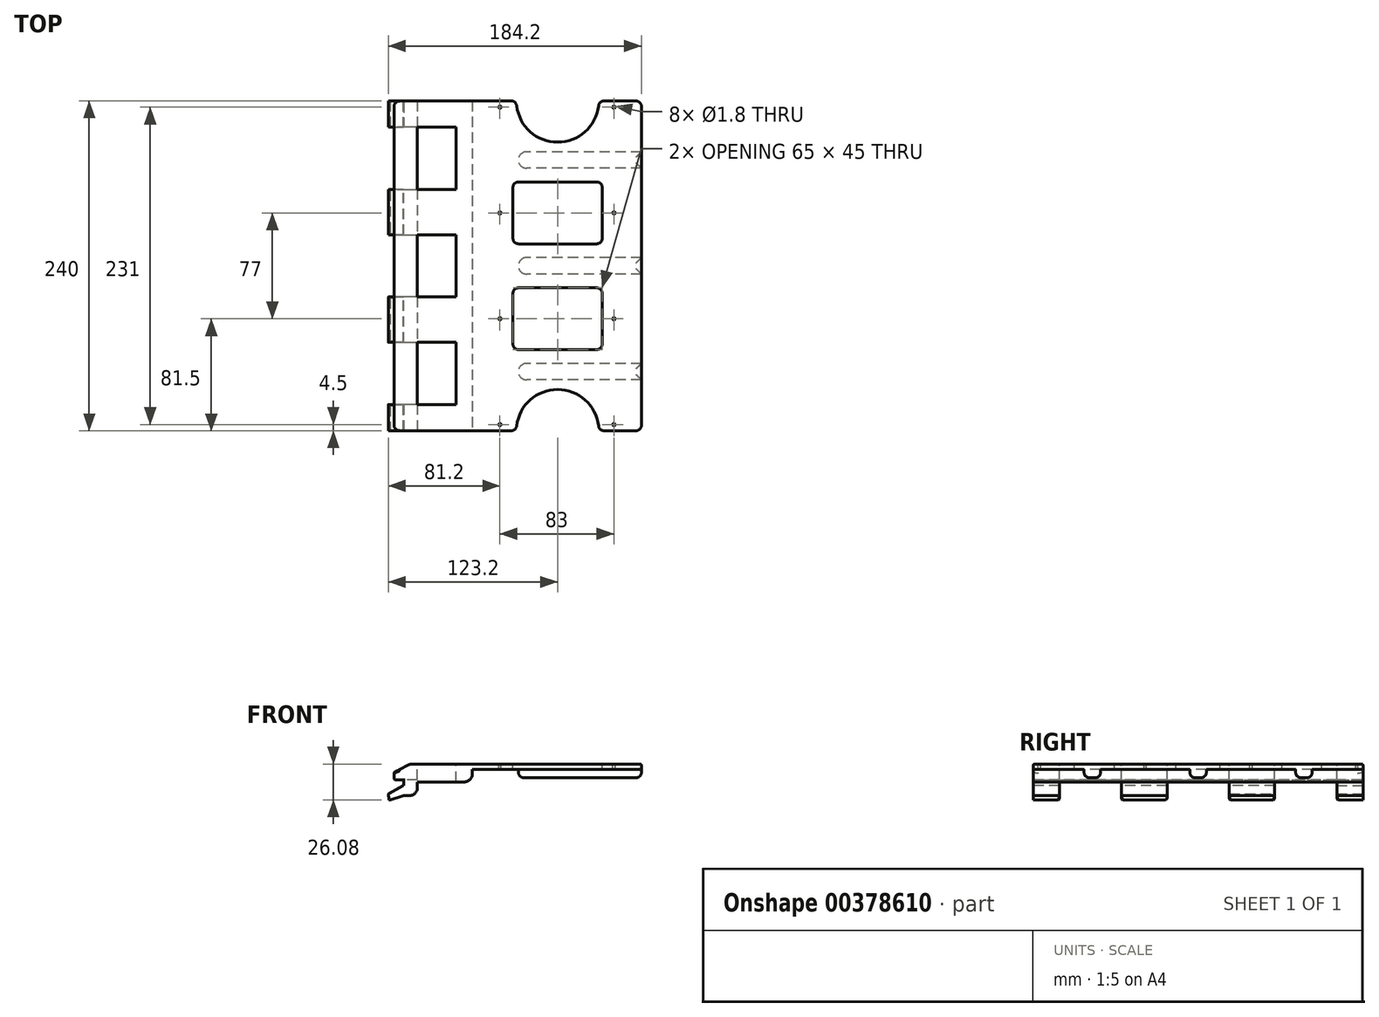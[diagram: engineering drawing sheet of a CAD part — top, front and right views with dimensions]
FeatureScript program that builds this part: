
annotation { "Feature Type Name" : "Feature", "Feature Type Description" : "" }
export const myFeature = defineFeature(function(context is Context, id is Id, definition is map)
    precondition{}
    {
        {
            var Q0;
            Q0=qCreatedBy(makeId("Top.planeOp"),FACE);
            var sketch = newSketch(context, id + "F0", { "sketchPlane" : qUnion([Q0])});
            skLineSegment(sketch, "E0", {"start": v(0, -197) * mm, "end": v(180, -197) * mm, "construction": true});
            skLineSegment(sketch, "E1", {"start": v(0, -43) * mm, "end": v(180, -43) * mm, "construction": true});
            skLineSegment(sketch, "E2", {"start": v(0, -158.5) * mm, "end": v(180, -158.5) * mm, "construction": true});
            skLineSegment(sketch, "E3", {"start": v(0, -81.5) * mm, "end": v(180, -81.5) * mm, "construction": true});
            skLineSegment(sketch, "E4", {"start": v(180, -203) * mm, "end": v(96.5, -203) * mm});
            skLineSegment(sketch, "E5", {"start": v(180, -191) * mm, "end": v(96.5, -191) * mm});
            skArc(sketch, "E6", {"start": v(96.5, -191) * mm, "mid": v(90.5, -197) * mm, "end": v(96.5, -203) * mm});
            skLineSegment(sketch, "E7", {"start": v(180, -126) * mm, "end": v(96.5, -126) * mm});
            skLineSegment(sketch, "E8", {"start": v(180, -114) * mm, "end": v(96.5, -114) * mm});
            skArc(sketch, "E9", {"start": v(96.5, -114) * mm, "mid": v(90.5, -120) * mm, "end": v(96.5, -126) * mm});
            skLineSegment(sketch, "E10", {"start": v(180, -49) * mm, "end": v(96.5, -49) * mm});
            skLineSegment(sketch, "E11", {"start": v(180, -37) * mm, "end": v(96.5, -37) * mm});
            skArc(sketch, "E12", {"start": v(96.5, -37) * mm, "mid": v(90.5, -43) * mm, "end": v(96.5, -49) * mm});
            skLineSegment(sketch, "E13", {"start": v(96.5, -240) * mm, "end": v(96.5, 0) * mm, "construction": true});
            skCircle(sketch, "E14", {"center": v(77, -158.5) * mm, "radius": 0.9 * mm});
            skCircle(sketch, "E15", {"center": v(77, -81.5) * mm, "radius": 0.9 * mm});
            skCircle(sketch, "E16", {"center": v(160, -158.5) * mm, "radius": 0.9 * mm});
            skCircle(sketch, "E17", {"center": v(160, -81.5) * mm, "radius": 0.9 * mm});
            skLineSegment(sketch, "E18.bottom", {"start": v(180, -240) * mm, "end": v(0, -240) * mm});
            skLineSegment(sketch, "E18.top", {"start": v(180, 0) * mm, "end": v(0, 0) * mm});
            skLineSegment(sketch, "E18.left", {"start": v(180, -240) * mm, "end": v(180, 0) * mm});
            skLineSegment(sketch, "E18.right", {"start": v(0, -240) * mm, "end": v(0, 0) * mm});
            skLineSegment(sketch, "E19", {"start": v(5, 0) * mm, "end": v(5, -240) * mm});
            skLineSegment(sketch, "E20", {"start": v(0, -120) * mm, "end": v(180, -120) * mm, "construction": true});
            skLineSegment(sketch, "E21", {"start": v(17, 0) * mm, "end": v(17, -240) * mm});
            skLineSegment(sketch, "E22", {"start": v(57, 0) * mm, "end": v(57, -240) * mm});
            skLineSegment(sketch, "E23", {"start": v(0, -97.4) * mm, "end": v(45, -97.4) * mm});
            skLineSegment(sketch, "E24", {"start": v(45, -97.4) * mm, "end": v(45, -142.6) * mm});
            skLineSegment(sketch, "E25", {"start": v(45, -142.6) * mm, "end": v(0, -142.6) * mm});
            skLineSegment(sketch, "E26", {"start": v(0, -175.7) * mm, "end": v(45, -175.7) * mm});
            skLineSegment(sketch, "E27", {"start": v(45, -175.7) * mm, "end": v(45, -220.9) * mm});
            skLineSegment(sketch, "E28", {"start": v(45, -220.9) * mm, "end": v(0, -220.9) * mm});
            skLineSegment(sketch, "E29", {"start": v(0, -64.3) * mm, "end": v(45, -64.3) * mm});
            skLineSegment(sketch, "E30", {"start": v(45, -64.3) * mm, "end": v(45, -19.1) * mm});
            skLineSegment(sketch, "E31", {"start": v(45, -19.1) * mm, "end": v(0, -19.1) * mm});
            skLineSegment(sketch, "E32", {"start": v(0, -235.5) * mm, "end": v(180, -235.5) * mm, "construction": true});
            skLineSegment(sketch, "E33", {"start": v(0, -4.5) * mm, "end": v(180, -4.5) * mm, "construction": true});
            skCircle(sketch, "E34", {"center": v(77, -235.5) * mm, "radius": 0.9 * mm});
            skCircle(sketch, "E35", {"center": v(77, -4.5) * mm, "radius": 0.9 * mm});
            skCircle(sketch, "E36", {"center": v(160, -4.5) * mm, "radius": 0.9 * mm});
            skCircle(sketch, "E37", {"center": v(160, -235.5) * mm, "radius": 0.9 * mm});
            skLineSegment(sketch, "E38.bottom", {"start": v(151.5, -104) * mm, "end": v(86.5, -104) * mm});
            skLineSegment(sketch, "E38.top", {"start": v(151.5, -59) * mm, "end": v(86.5, -59) * mm});
            skLineSegment(sketch, "E38.left", {"start": v(151.5, -104) * mm, "end": v(151.5, -59) * mm});
            skLineSegment(sketch, "E38.right", {"start": v(86.5, -104) * mm, "end": v(86.5, -59) * mm});
            skPoint(sketch, "E38.middle", {"position": v(119, -81.5) * mm});
            skLineSegment(sketch, "E39.bottom", {"start": v(151.5, -181) * mm, "end": v(86.5, -181) * mm});
            skLineSegment(sketch, "E39.top", {"start": v(151.5, -136) * mm, "end": v(86.5, -136) * mm});
            skLineSegment(sketch, "E39.left", {"start": v(151.5, -181) * mm, "end": v(151.5, -136) * mm});
            skLineSegment(sketch, "E39.right", {"start": v(86.5, -181) * mm, "end": v(86.5, -136) * mm});
            skPoint(sketch, "E39.middle", {"position": v(119, -158.5) * mm});
            skCircle(sketch, "E40", {"center": v(119, 0) * mm, "radius": 30 * mm});
            skCircle(sketch, "E41", {"center": v(119, -240) * mm, "radius": 30 * mm});
            skPoint(sketch, "E41.centerSnap0", {"position": v(119, -181) * mm});
            skSolve(sketch);
        }
        {
            var Q0;
            {var subQ7=sQuery(id+"F0.wireOp",EDGE,"E4");Q0=makeQuery(id+"F0.imprint","IMPRINT",FACE,{"disambiguationData":[TD([[makeQuery(id+"F0.imprint","IMPRINT",EDGE,{"derivedFrom":subQ7}),1.0]])]});}
            var Q1;
            {var subQ0=sQuery(id+"F0.wireOp",EDGE,"E4");Q1=makeQuery(id+"F0.imprint","IMPRINT",FACE,{"disambiguationData":[TD([[makeQuery(id+"F0.imprint","IMPRINT",EDGE,{"derivedFrom":subQ0}),-1.0]])]});}
            var Q2;
            {var subQ0=sQuery(id+"F0.wireOp",EDGE,"E7");Q2=makeQuery(id+"F0.imprint","IMPRINT",FACE,{"disambiguationData":[TD([[makeQuery(id+"F0.imprint","IMPRINT",EDGE,{"derivedFrom":subQ0}),-1.0]])]});}
            var Q3;
            {var subQ0=sQuery(id+"F0.wireOp",EDGE,"E10");Q3=makeQuery(id+"F0.imprint","IMPRINT",FACE,{"disambiguationData":[TD([[makeQuery(id+"F0.imprint","IMPRINT",EDGE,{"derivedFrom":subQ0}),-1.0]])]});}
            extrude(context, id + "F1", {"entities" : qUnion([Q0, Q1, Q2, Q3]), "oppositeDirection" : true, "depth" : 4 * mm});
        }
        {
            var Q0;
            {var subQ0=sQuery(id+"F0.wireOp",EDGE,"E21");Q0=makeQuery(id+"F0.imprint","IMPRINT",FACE,{"disambiguationData":[TD([[makeQuery(id+"F0.imprint","IMPRINT",EDGE,{"derivedFrom":subQ0}),1.0]])]});}
            var Q1;
            {var subQ5=sQuery(id+"F0.wireOp",EDGE,"n4lQ4PQO-9XsQ-tz0W-XekK-HpTfJCge4sbG");Q1=makeQuery(id+"F0.imprint","IMPRINT",FACE,{"disambiguationData":[TD([[makeQuery(id+"F0.imprint","IMPRINT",EDGE,{"derivedFrom":subQ5}),1.0]])]});}
            var Q2;
            {var subQ5=sQuery(id+"F0.wireOp",EDGE,"NRY2d1nv-D3un-2PJu-Z2eF-jLOu5DY2E8th");Q2=makeQuery(id+"F0.imprint","IMPRINT",FACE,{"disambiguationData":[TD([[makeQuery(id+"F0.imprint","IMPRINT",EDGE,{"derivedFrom":subQ5}),1.0]])]});}
            extrude(context, id + "F2", {"entities" : qUnion([Q0, Q1, Q2]), "operationType" : NewBodyOperationType.ADD, "oppositeDirection" : true, "depth" : 13 * mm});
        }
        {
            var Q0;
            {var subQ0=sQuery(id+"F0.wireOp",EDGE,"E19");var subQ1=sQuery(id+"F0.wireOp",EDGE,"E18.bottom");var subQ2=makeQuery(id+"F0.imprint","INTERSECT",VERTEX,{"derivedFrom":[subQ1,subQ0]});Q0=makeQuery(id+"F0.imprint","IMPRINT",FACE,{"disambiguationData":[TD([[makeQuery(id+"F0.imprint","IMPRINT",EDGE,{"disambiguationData":[TD([[subQ2,1.0]])],"derivedFrom":subQ1}),-1.0]])]});}
            var Q1;
            {var subQ0=sQuery(id+"F0.wireOp",EDGE,"E19");var subQ1=sQuery(id+"F0.wireOp",EDGE,"E18.top");var subQ2=makeQuery(id+"F0.imprint","INTERSECT",VERTEX,{"derivedFrom":[subQ1,subQ0]});Q1=makeQuery(id+"F0.imprint","IMPRINT",FACE,{"disambiguationData":[TD([[makeQuery(id+"F0.imprint","IMPRINT",EDGE,{"disambiguationData":[TD([[subQ2,1.0]])],"derivedFrom":subQ1}),1.0]])]});}
            var Q2;
            {var subQ0=sQuery(id+"F0.wireOp",EDGE,"E29");var subQ1=sQuery(id+"F0.wireOp",EDGE,"E19");var subQ2=makeQuery(id+"F0.imprint","INTERSECT",VERTEX,{"derivedFrom":[subQ1,subQ0]});Q2=makeQuery(id+"F0.imprint","IMPRINT",FACE,{"disambiguationData":[TD([[makeQuery(id+"F0.imprint","IMPRINT",EDGE,{"disambiguationData":[TD([[subQ2,-1.0]])],"derivedFrom":subQ1}),1.0]])]});}
            var Q3;
            {var subQ0=sQuery(id+"F0.wireOp",EDGE,"E25");var subQ1=sQuery(id+"F0.wireOp",EDGE,"E19");var subQ2=makeQuery(id+"F0.imprint","INTERSECT",VERTEX,{"derivedFrom":[subQ1,subQ0]});Q3=makeQuery(id+"F0.imprint","IMPRINT",FACE,{"disambiguationData":[TD([[makeQuery(id+"F0.imprint","IMPRINT",EDGE,{"disambiguationData":[TD([[subQ2,-1.0]])],"derivedFrom":subQ1}),1.0]])]});}
            extrude(context, id + "F3", {"entities" : qUnion([Q0, Q1, Q2, Q3]), "operationType" : NewBodyOperationType.ADD, "oppositeDirection" : true, "depth" : 23 * mm});
        }
        {
            var Q0;
            {var subQ0=sQuery(id+"F0.wireOp",EDGE,"E18.right");var subQ1=sQuery(id+"F0.wireOp",EDGE,"E18.bottom");var subQ2=makeQuery(id+"F0.imprint","INTERSECT",VERTEX,{"derivedFrom":[subQ1,subQ0]});Q0=makeQuery(id+"F0.imprint","IMPRINT",FACE,{"disambiguationData":[TD([[makeQuery(id+"F0.imprint","IMPRINT",EDGE,{"disambiguationData":[TD([[subQ2,1.0]])],"derivedFrom":subQ1}),-1.0]])]});}
            var Q1;
            {var subQ0=sQuery(id+"F0.wireOp",EDGE,"E18.right");var subQ1=sQuery(id+"F0.wireOp",EDGE,"E18.top");var subQ2=makeQuery(id+"F0.imprint","INTERSECT",VERTEX,{"derivedFrom":[subQ1,subQ0]});Q1=makeQuery(id+"F0.imprint","IMPRINT",FACE,{"disambiguationData":[TD([[makeQuery(id+"F0.imprint","IMPRINT",EDGE,{"disambiguationData":[TD([[subQ2,1.0]])],"derivedFrom":subQ1}),1.0]])]});}
            var Q2;
            {var subQ0=sQuery(id+"F0.wireOp",EDGE,"E25");var subQ1=sQuery(id+"F0.wireOp",EDGE,"E18.right");var subQ2=makeQuery(id+"F0.imprint","INTERSECT",VERTEX,{"derivedFrom":[subQ1,subQ0]});Q2=makeQuery(id+"F0.imprint","IMPRINT",FACE,{"disambiguationData":[TD([[makeQuery(id+"F0.imprint","IMPRINT",EDGE,{"disambiguationData":[TD([[subQ2,1.0]])],"derivedFrom":subQ1}),-1.0]])]});}
            var Q3;
            {var subQ0=sQuery(id+"F0.wireOp",EDGE,"E23");var subQ1=sQuery(id+"F0.wireOp",EDGE,"E18.right");var subQ2=makeQuery(id+"F0.imprint","INTERSECT",VERTEX,{"derivedFrom":[subQ1,subQ0]});Q3=makeQuery(id+"F0.imprint","IMPRINT",FACE,{"disambiguationData":[TD([[makeQuery(id+"F0.imprint","IMPRINT",EDGE,{"disambiguationData":[TD([[subQ2,-1.0]])],"derivedFrom":subQ1}),-1.0]])]});}
            var Q4;
            {var subQ0=sQuery(id+"F0.wireOp",EDGE,"E26");var subQ1=sQuery(id+"F0.wireOp",EDGE,"E18.right");var subQ2=makeQuery(id+"F0.imprint","INTERSECT",VERTEX,{"derivedFrom":[subQ1,subQ0]});Q4=makeQuery(id+"F0.imprint","IMPRINT",FACE,{"disambiguationData":[TD([[makeQuery(id+"F0.imprint","IMPRINT",EDGE,{"disambiguationData":[TD([[subQ2,1.0]])],"derivedFrom":subQ1}),-1.0]])]});}
            var Q5;
            {var subQ0=sQuery(id+"F0.wireOp",EDGE,"E23");var subQ1=sQuery(id+"F0.wireOp",EDGE,"E18.right");var subQ2=makeQuery(id+"F0.imprint","INTERSECT",VERTEX,{"derivedFrom":[subQ1,subQ0]});Q5=makeQuery(id+"F0.imprint","IMPRINT",FACE,{"disambiguationData":[TD([[makeQuery(id+"F0.imprint","IMPRINT",EDGE,{"disambiguationData":[TD([[subQ2,1.0]])],"derivedFrom":subQ1}),-1.0]])]});}
            var Q6;
            {var subQ0=sQuery(id+"F0.wireOp",EDGE,"E29");var subQ1=sQuery(id+"F0.wireOp",EDGE,"E18.right");var subQ2=makeQuery(id+"F0.imprint","INTERSECT",VERTEX,{"derivedFrom":[subQ1,subQ0]});Q6=makeQuery(id+"F0.imprint","IMPRINT",FACE,{"disambiguationData":[TD([[makeQuery(id+"F0.imprint","IMPRINT",EDGE,{"disambiguationData":[TD([[subQ2,-1.0]])],"derivedFrom":subQ1}),-1.0]])]});}
            var Q7;
            {var subQ0=sQuery(id+"F0.wireOp",EDGE,"E26");var subQ1=sQuery(id+"F0.wireOp",EDGE,"E19");var subQ2=makeQuery(id+"F0.imprint","INTERSECT",VERTEX,{"derivedFrom":[subQ1,subQ0]});Q7=makeQuery(id+"F0.imprint","IMPRINT",FACE,{"disambiguationData":[TD([[makeQuery(id+"F0.imprint","IMPRINT",EDGE,{"disambiguationData":[TD([[subQ2,-1.0]])],"derivedFrom":subQ1}),1.0]])]});}
            var Q8;
            {var subQ0=sQuery(id+"F0.wireOp",EDGE,"E23");var subQ1=sQuery(id+"F0.wireOp",EDGE,"E19");var subQ2=makeQuery(id+"F0.imprint","INTERSECT",VERTEX,{"derivedFrom":[subQ1,subQ0]});Q8=makeQuery(id+"F0.imprint","IMPRINT",FACE,{"disambiguationData":[TD([[makeQuery(id+"F0.imprint","IMPRINT",EDGE,{"disambiguationData":[TD([[subQ2,-1.0]])],"derivedFrom":subQ1}),1.0]])]});}
            var Q9;
            {var subQ0=sQuery(id+"F0.wireOp",EDGE,"E31");var subQ1=sQuery(id+"F0.wireOp",EDGE,"E19");var subQ2=makeQuery(id+"F0.imprint","INTERSECT",VERTEX,{"derivedFrom":[subQ1,subQ0]});Q9=makeQuery(id+"F0.imprint","IMPRINT",FACE,{"disambiguationData":[TD([[makeQuery(id+"F0.imprint","IMPRINT",EDGE,{"disambiguationData":[TD([[subQ2,-1.0]])],"derivedFrom":subQ1}),1.0]])]});}
            var Q10;
            Q10=makeQuery(id+"F2.opExtrude","CAP_FACE",FACE,{"disambiguationData":[OSD([sQuery(id+"F0.wireOp",EDGE,"E14"),sQuery(id+"F0.wireOp",EDGE,"E15"),sQuery(id+"F0.wireOp",EDGE,"E18.bottom"),sQuery(id+"F0.wireOp",EDGE,"E18.top"),sQuery(id+"F0.wireOp",EDGE,"E21"),sQuery(id+"F0.wireOp",EDGE,"E22")])],"isStart":false});
            extrude(context, id + "F4", {"entities" : qUnion([Q0, Q1, Q2, Q3, Q4, Q5, Q6, Q7, Q8, Q9]), "operationType" : NewBodyOperationType.ADD, "oppositeDirection" : true, "endBoundEntityFace" : qUnion([Q10]), "depth" : 11.5 * mm});
        }
        {
            var Q0;
            {var subQ0=sQuery(id+"F0.wireOp",EDGE,"E18.bottom");Q0=makeQuery(id+"F4.boolean.opBoolean","MERGE",FACE,{"derivedFrom":[makeQuery(id+"F3.boolean.opBoolean","MERGE",FACE,{"derivedFrom":[makeQuery(id+"F2.boolean.opBoolean","MERGE",FACE,{"derivedFrom":[makeQuery(id+"F1.opExtrude","SWEPT_FACE",FACE,{"disambiguationData":[OSD([subQ0])]}),makeQuery(id+"F2.opExtrude","SWEPT_FACE",FACE,{"disambiguationData":[OSD([subQ0])]})]}),makeQuery(id+"F3.opExtrude","SWEPT_FACE",FACE,{"disambiguationData":[OSD([subQ0])]})]}),makeQuery(id+"F4.opExtrude","SWEPT_FACE",FACE,{"disambiguationData":[OSD([subQ0])]})]});}
            var sketch = newSketch(context, id + "F5", { "sketchPlane" : qUnion([Q0])});
            skLineSegment(sketch, "E42.bottom", {"start": v(5, -11.5) * mm, "end": v(7, -11.5) * mm});
            skLineSegment(sketch, "E42.top", {"start": v(5, -15.5) * mm, "end": v(7, -15.5) * mm});
            skLineSegment(sketch, "E42.left", {"start": v(5, -11.5) * mm, "end": v(5, -15.5) * mm});
            skLineSegment(sketch, "E42.right", {"start": v(7, -11.5) * mm, "end": v(7, -15.5) * mm});
            skSolve(sketch);
        }
        {
            var Q0;
            Q0=makeQuery(id+"F5.imprint","IMPRINT",FACE,{"disambiguationData":[TD([[makeQuery(id+"F5.imprint","IMPRINT",EDGE,{"derivedFrom":sQuery(id+"F5.wireOp",EDGE,"E42.bottom")}),-1.0]])]});
            var Q1;
            {var subQ0=sQuery(id+"F0.wireOp",EDGE,"E18.top");Q1=makeQuery(id+"F4.boolean.opBoolean","MERGE",FACE,{"derivedFrom":[makeQuery(id+"F3.boolean.opBoolean","MERGE",FACE,{"derivedFrom":[makeQuery(id+"F2.boolean.opBoolean","MERGE",FACE,{"derivedFrom":[makeQuery(id+"F1.opExtrude","SWEPT_FACE",FACE,{"disambiguationData":[OSD([subQ0])]}),makeQuery(id+"F2.opExtrude","SWEPT_FACE",FACE,{"disambiguationData":[OSD([subQ0])]})]}),makeQuery(id+"F3.opExtrude","SWEPT_FACE",FACE,{"disambiguationData":[OSD([subQ0])]})]}),makeQuery(id+"F4.opExtrude","SWEPT_FACE",FACE,{"disambiguationData":[OSD([subQ0])]})]});}
            extrude(context, id + "F6", {"entities" : qUnion([Q0]), "operationType" : NewBodyOperationType.REMOVE, "oppositeDirection" : true, "endBoundEntityFace" : qUnion([Q1]), "depth" : 300 * mm});
        }
        {
            var Q0;
            {var subQ0=sQuery(id+"F0.wireOp",EDGE,"E4");Q0=makeQuery(id+"F0.imprint","IMPRINT",FACE,{"disambiguationData":[TD([[makeQuery(id+"F0.imprint","IMPRINT",EDGE,{"derivedFrom":subQ0}),-1.0]])]});}
            var Q1;
            {var subQ0=sQuery(id+"F0.wireOp",EDGE,"E7");Q1=makeQuery(id+"F0.imprint","IMPRINT",FACE,{"disambiguationData":[TD([[makeQuery(id+"F0.imprint","IMPRINT",EDGE,{"derivedFrom":subQ0}),-1.0]])]});}
            var Q2;
            {var subQ0=sQuery(id+"F0.wireOp",EDGE,"E10");Q2=makeQuery(id+"F0.imprint","IMPRINT",FACE,{"disambiguationData":[TD([[makeQuery(id+"F0.imprint","IMPRINT",EDGE,{"derivedFrom":subQ0}),-1.0]])]});}
            extrude(context, id + "F7", {"entities" : qUnion([Q0, Q1, Q2]), "operationType" : NewBodyOperationType.ADD, "oppositeDirection" : true, "depth" : 10 * mm});
        }
        {
            var Q0;
            Q0=makeQuery(id+"F7.opExtrude","CAP_FACE",FACE,{"disambiguationData":[OSD([sQuery(id+"F0.wireOp",EDGE,"E10"),sQuery(id+"F0.wireOp",EDGE,"E11"),sQuery(id+"F0.wireOp",EDGE,"E12"),sQuery(id+"F0.wireOp",EDGE,"E18.left")])],"isStart":false});
            var Q1;
            Q1=makeQuery(id+"F7.opExtrude","CAP_FACE",FACE,{"disambiguationData":[OSD([sQuery(id+"F0.wireOp",EDGE,"E7"),sQuery(id+"F0.wireOp",EDGE,"E8"),sQuery(id+"F0.wireOp",EDGE,"E9"),sQuery(id+"F0.wireOp",EDGE,"E18.left")])],"isStart":false});
            var Q2;
            Q2=makeQuery(id+"F7.opExtrude","CAP_FACE",FACE,{"disambiguationData":[OSD([sQuery(id+"F0.wireOp",EDGE,"E4"),sQuery(id+"F0.wireOp",EDGE,"E5"),sQuery(id+"F0.wireOp",EDGE,"E6"),sQuery(id+"F0.wireOp",EDGE,"E18.left")])],"isStart":false});
            var Q3;
            Q3=makeQuery(id+"F1.opExtrude","SWEPT_EDGE",EDGE,{"disambiguationData":[OSD([sQuery(id+"F0.wireOp",EDGE,"E38.top"),sQuery(id+"F0.wireOp",EDGE,"E38.right")])]});
            var Q4;
            Q4=makeQuery(id+"F1.opExtrude","SWEPT_EDGE",EDGE,{"disambiguationData":[OSD([sQuery(id+"F0.wireOp",EDGE,"E38.bottom"),sQuery(id+"F0.wireOp",EDGE,"E38.right")])]});
            var Q5;
            Q5=makeQuery(id+"F1.opExtrude","SWEPT_EDGE",EDGE,{"disambiguationData":[OSD([sQuery(id+"F0.wireOp",EDGE,"E38.top"),sQuery(id+"F0.wireOp",EDGE,"E38.left")])]});
            var Q6;
            Q6=makeQuery(id+"F1.opExtrude","SWEPT_EDGE",EDGE,{"disambiguationData":[OSD([sQuery(id+"F0.wireOp",EDGE,"E38.bottom"),sQuery(id+"F0.wireOp",EDGE,"E38.left")])]});
            var Q7;
            Q7=makeQuery(id+"F1.opExtrude","SWEPT_EDGE",EDGE,{"disambiguationData":[OSD([sQuery(id+"F0.wireOp",EDGE,"E39.top"),sQuery(id+"F0.wireOp",EDGE,"E39.left")])]});
            var Q8;
            {var subQ0=sQuery(id+"F0.wireOp",EDGE,"E41");var subQ1=sQuery(id+"F0.wireOp",EDGE,"E18.bottom");Q8=makeQuery(id+"F1.opExtrude","SWEPT_EDGE",EDGE,{"disambiguationData":[OSD([subQ1,subQ0]),TDD([makeQuery(id+"F0.imprint","INTERSECT",VERTEX,{"disambiguationData":[OD(1.0)],"derivedFrom":[subQ1,subQ0]})])]});}
            var Q9;
            Q9=makeQuery(id+"F1.opExtrude","SWEPT_EDGE",EDGE,{"disambiguationData":[OSD([sQuery(id+"F0.wireOp",EDGE,"E39.bottom"),sQuery(id+"F0.wireOp",EDGE,"E39.right")])]});
            var Q10;
            Q10=makeQuery(id+"F1.opExtrude","SWEPT_EDGE",EDGE,{"disambiguationData":[OSD([sQuery(id+"F0.wireOp",EDGE,"E39.top"),sQuery(id+"F0.wireOp",EDGE,"E39.right")])]});
            var Q11;
            {var subQ0=sQuery(id+"F0.wireOp",EDGE,"E40");var subQ1=sQuery(id+"F0.wireOp",EDGE,"E18.top");Q11=makeQuery(id+"F1.opExtrude","SWEPT_EDGE",EDGE,{"disambiguationData":[OSD([subQ1,subQ0]),TDD([makeQuery(id+"F0.imprint","INTERSECT",VERTEX,{"disambiguationData":[OD(1.0)],"derivedFrom":[subQ1,subQ0]})])]});}
            var Q12;
            {var subQ0=sQuery(id+"F0.wireOp",EDGE,"E40");var subQ1=sQuery(id+"F0.wireOp",EDGE,"E18.top");Q12=makeQuery(id+"F1.opExtrude","SWEPT_EDGE",EDGE,{"disambiguationData":[OSD([subQ1,subQ0]),TDD([makeQuery(id+"F0.imprint","INTERSECT",VERTEX,{"disambiguationData":[OD(0.0)],"derivedFrom":[subQ1,subQ0]})])]});}
            var Q13;
            Q13=makeQuery(id+"F1.opExtrude","SWEPT_EDGE",EDGE,{"disambiguationData":[OSD([sQuery(id+"F0.wireOp",EDGE,"E39.bottom"),sQuery(id+"F0.wireOp",EDGE,"E39.left")])]});
            var Q14;
            {var subQ0=sQuery(id+"F0.wireOp",EDGE,"E41");var subQ1=sQuery(id+"F0.wireOp",EDGE,"E18.bottom");Q14=makeQuery(id+"F1.opExtrude","SWEPT_EDGE",EDGE,{"disambiguationData":[OSD([subQ1,subQ0]),TDD([makeQuery(id+"F0.imprint","INTERSECT",VERTEX,{"disambiguationData":[OD(0.0)],"derivedFrom":[subQ1,subQ0]})])]});}
            var Q15;
            Q15=makeQuery(id+"F1.opExtrude","SWEPT_EDGE",EDGE,{"disambiguationData":[OSD([sQuery(id+"F0.wireOp",EDGE,"E18.bottom"),sQuery(id+"F0.wireOp",EDGE,"E18.left")])]});
            var Q16;
            Q16=makeQuery(id+"F1.opExtrude","SWEPT_EDGE",EDGE,{"disambiguationData":[OSD([sQuery(id+"F0.wireOp",EDGE,"E18.top"),sQuery(id+"F0.wireOp",EDGE,"E18.left")])]});
            var Q17;
            Q17=makeQuery(id+"F4.opExtrude","SWEPT_EDGE",EDGE,{"disambiguationData":[OSD([sQuery(id+"F0.wireOp",EDGE,"E18.top"),sQuery(id+"F0.wireOp",EDGE,"E18.right")])]});
            var Q18;
            Q18=makeQuery(id+"F4.opExtrude","SWEPT_EDGE",EDGE,{"disambiguationData":[OSD([sQuery(id+"F0.wireOp",EDGE,"E18.bottom"),sQuery(id+"F0.wireOp",EDGE,"E18.right")])]});
            fillet(context, id + "F8", {"entities" : qUnion([Q0, Q1, Q2, Q3, Q4, Q5, Q6, Q7, Q8, Q9, Q10, Q11, Q12, Q13, Q14, Q15, Q16, Q17, Q18]), "radius" : 4 * mm, "tangentPropagation" : true, "allowEdgeOverflow" : false});
        }
        {
            var Q0;
            Q0=makeQuery(id+"F4.opExtrude","CAP_EDGE",EDGE,{"disambiguationData":[OSD([sQuery(id+"F0.wireOp",EDGE,"E18.right")])],"isStart":true});
            chamfer(context, id + "F9", {"entities" : qUnion([Q0]), "chamferType" : ChamferType.TWO_OFFSETS, "width1" : 6 * mm, "oppositeDirection" : false, "width2" : 12 * mm});
        }
        {
            var Q0;
            {var subQ0=sQuery(id+"F0.wireOp",EDGE,"E19");Q0=makeQuery(id+"F3.opExtrude","CAP_EDGE",EDGE,{"disambiguationData":[OSD([subQ0]),TDD([makeQuery(id+"F0.imprint","IMPRINT",EDGE,{"disambiguationData":[TD([[makeQuery(id+"F0.imprint","INTERSECT",VERTEX,{"derivedFrom":[sQuery(id+"F0.wireOp",EDGE,"E18.bottom"),subQ0]}),1.0]])],"derivedFrom":subQ0})])],"isStart":false});}
            var Q1;
            {var subQ0=sQuery(id+"F0.wireOp",EDGE,"E19");Q1=makeQuery(id+"F3.opExtrude","CAP_EDGE",EDGE,{"disambiguationData":[OSD([subQ0]),TDD([makeQuery(id+"F0.imprint","IMPRINT",EDGE,{"disambiguationData":[TD([[makeQuery(id+"F0.imprint","INTERSECT",VERTEX,{"derivedFrom":[subQ0,sQuery(id+"F0.wireOp",EDGE,"E25")]}),-1.0]])],"derivedFrom":subQ0})])],"isStart":false});}
            var Q2;
            {var subQ0=sQuery(id+"F0.wireOp",EDGE,"E19");Q2=makeQuery(id+"F3.opExtrude","CAP_EDGE",EDGE,{"disambiguationData":[OSD([subQ0]),TDD([makeQuery(id+"F0.imprint","IMPRINT",EDGE,{"disambiguationData":[TD([[makeQuery(id+"F0.imprint","INTERSECT",VERTEX,{"derivedFrom":[subQ0,sQuery(id+"F0.wireOp",EDGE,"E29")]}),-1.0]])],"derivedFrom":subQ0})])],"isStart":false});}
            var Q3;
            {var subQ0=sQuery(id+"F0.wireOp",EDGE,"E19");Q3=makeQuery(id+"F3.opExtrude","CAP_EDGE",EDGE,{"disambiguationData":[OSD([subQ0]),TDD([makeQuery(id+"F0.imprint","IMPRINT",EDGE,{"disambiguationData":[TD([[makeQuery(id+"F0.imprint","INTERSECT",VERTEX,{"derivedFrom":[sQuery(id+"F0.wireOp",EDGE,"E18.top"),subQ0]}),-1.0]])],"derivedFrom":subQ0})])],"isStart":false});}
            chamfer(context, id + "F10", {"entities" : qUnion([Q0, Q1, Q2, Q3]), "chamferType" : ChamferType.TWO_OFFSETS, "width1" : 20 * mm, "oppositeDirection" : false, "width2" : 2 * mm});
        }
        {
            var Q0;
            {var subQ0=sQuery(id+"F0.wireOp",EDGE,"E19");Q0=makeQuery(id+"F10.opChamfer","BLEND_FACE",FACE,{"disambiguationData":[OSD([subQ0]),TDD([makeQuery(id+"F3.opExtrude","CAP_EDGE",EDGE,{"disambiguationData":[OSD([subQ0]),TDD([makeQuery(id+"F0.imprint","IMPRINT",EDGE,{"disambiguationData":[TD([[makeQuery(id+"F0.imprint","INTERSECT",VERTEX,{"derivedFrom":[sQuery(id+"F0.wireOp",EDGE,"E18.bottom"),subQ0]}),1.0]])],"derivedFrom":subQ0})])],"isStart":false})])]});}
            var Q1;
            {var subQ0=sQuery(id+"F0.wireOp",EDGE,"E19");Q1=makeQuery(id+"F10.opChamfer","BLEND_FACE",FACE,{"disambiguationData":[OSD([subQ0]),TDD([makeQuery(id+"F3.opExtrude","CAP_EDGE",EDGE,{"disambiguationData":[OSD([subQ0]),TDD([makeQuery(id+"F0.imprint","IMPRINT",EDGE,{"disambiguationData":[TD([[makeQuery(id+"F0.imprint","INTERSECT",VERTEX,{"derivedFrom":[subQ0,sQuery(id+"F0.wireOp",EDGE,"E25")]}),-1.0]])],"derivedFrom":subQ0})])],"isStart":false})])]});}
            var Q2;
            {var subQ0=sQuery(id+"F0.wireOp",EDGE,"E19");Q2=makeQuery(id+"F10.opChamfer","BLEND_FACE",FACE,{"disambiguationData":[OSD([subQ0]),TDD([makeQuery(id+"F3.opExtrude","CAP_EDGE",EDGE,{"disambiguationData":[OSD([subQ0]),TDD([makeQuery(id+"F0.imprint","IMPRINT",EDGE,{"disambiguationData":[TD([[makeQuery(id+"F0.imprint","INTERSECT",VERTEX,{"derivedFrom":[subQ0,sQuery(id+"F0.wireOp",EDGE,"E29")]}),-1.0]])],"derivedFrom":subQ0})])],"isStart":false})])]});}
            var Q3;
            {var subQ0=sQuery(id+"F0.wireOp",EDGE,"E19");Q3=makeQuery(id+"F10.opChamfer","BLEND_FACE",FACE,{"disambiguationData":[OSD([subQ0]),TDD([makeQuery(id+"F3.opExtrude","CAP_EDGE",EDGE,{"disambiguationData":[OSD([subQ0]),TDD([makeQuery(id+"F0.imprint","IMPRINT",EDGE,{"disambiguationData":[TD([[makeQuery(id+"F0.imprint","INTERSECT",VERTEX,{"derivedFrom":[sQuery(id+"F0.wireOp",EDGE,"E18.top"),subQ0]}),-1.0]])],"derivedFrom":subQ0})])],"isStart":false})])]});}
            extrude(context, id + "F11", {"entities" : qUnion([Q0, Q1, Q2, Q3]), "operationType" : NewBodyOperationType.ADD, "depth" : 7 * mm});
        }
        {
            var Q0;
            {var subQ0=sQuery(id+"F0.wireOp",EDGE,"E19");Q0=makeQuery(id+"F11.opExtrude","CAP_FACE",FACE,{"disambiguationData":[OSD([subQ0]),TDD([makeQuery(id+"F10.opChamfer","BLEND_FACE",FACE,{"disambiguationData":[OSD([subQ0]),TDD([makeQuery(id+"F3.opExtrude","CAP_EDGE",EDGE,{"disambiguationData":[OSD([subQ0]),TDD([makeQuery(id+"F0.imprint","IMPRINT",EDGE,{"disambiguationData":[TD([[makeQuery(id+"F0.imprint","INTERSECT",VERTEX,{"derivedFrom":[sQuery(id+"F0.wireOp",EDGE,"E18.bottom"),subQ0]}),1.0]])],"derivedFrom":subQ0})])],"isStart":false})])]})])],"isStart":false});}
            var Q1;
            {var subQ0=sQuery(id+"F0.wireOp",EDGE,"E19");Q1=makeQuery(id+"F11.opExtrude","CAP_FACE",FACE,{"disambiguationData":[OSD([subQ0]),TDD([makeQuery(id+"F10.opChamfer","BLEND_FACE",FACE,{"disambiguationData":[OSD([subQ0]),TDD([makeQuery(id+"F3.opExtrude","CAP_EDGE",EDGE,{"disambiguationData":[OSD([subQ0]),TDD([makeQuery(id+"F0.imprint","IMPRINT",EDGE,{"disambiguationData":[TD([[makeQuery(id+"F0.imprint","INTERSECT",VERTEX,{"derivedFrom":[subQ0,sQuery(id+"F0.wireOp",EDGE,"E25")]}),-1.0]])],"derivedFrom":subQ0})])],"isStart":false})])]})])],"isStart":false});}
            var Q2;
            {var subQ0=sQuery(id+"F0.wireOp",EDGE,"E19");Q2=makeQuery(id+"F11.opExtrude","CAP_FACE",FACE,{"disambiguationData":[OSD([subQ0]),TDD([makeQuery(id+"F10.opChamfer","BLEND_FACE",FACE,{"disambiguationData":[OSD([subQ0]),TDD([makeQuery(id+"F3.opExtrude","CAP_EDGE",EDGE,{"disambiguationData":[OSD([subQ0]),TDD([makeQuery(id+"F0.imprint","IMPRINT",EDGE,{"disambiguationData":[TD([[makeQuery(id+"F0.imprint","INTERSECT",VERTEX,{"derivedFrom":[subQ0,sQuery(id+"F0.wireOp",EDGE,"E29")]}),-1.0]])],"derivedFrom":subQ0})])],"isStart":false})])]})])],"isStart":false});}
            var Q3;
            {var subQ0=sQuery(id+"F0.wireOp",EDGE,"E19");Q3=makeQuery(id+"F11.opExtrude","CAP_FACE",FACE,{"disambiguationData":[OSD([subQ0]),TDD([makeQuery(id+"F10.opChamfer","BLEND_FACE",FACE,{"disambiguationData":[OSD([subQ0]),TDD([makeQuery(id+"F3.opExtrude","CAP_EDGE",EDGE,{"disambiguationData":[OSD([subQ0]),TDD([makeQuery(id+"F0.imprint","IMPRINT",EDGE,{"disambiguationData":[TD([[makeQuery(id+"F0.imprint","INTERSECT",VERTEX,{"derivedFrom":[sQuery(id+"F0.wireOp",EDGE,"E18.top"),subQ0]}),-1.0]])],"derivedFrom":subQ0})])],"isStart":false})])]})])],"isStart":false});}
            extrude(context, id + "F12", {"entities" : qUnion([Q0, Q1, Q2, Q3]), "operationType" : NewBodyOperationType.ADD, "depth" : 4 * mm});
        }
        {
            var Q0;
            Q0=makeQuery(id+"F12.opExtrude","CAP_EDGE",EDGE,{"disambiguationData":[OSD([sQuery(id+"F0.wireOp",EDGE,"E19"),sQuery(id+"F5.wireOp",EDGE,"E42.top")])],"isStart":false});
            chamfer(context, id + "F13", {"entities" : qUnion([Q0]), "chamferType" : ChamferType.TWO_OFFSETS, "width1" : 11.5 * mm, "oppositeDirection" : false, "width2" : 5 * mm, "tangentPropagation" : true});
        }
        {
            var Q0;
            {var subQ0=sQuery(id+"F0.wireOp",EDGE,"E21");Q0=makeQuery(id+"F3.opExtrude","CAP_EDGE",EDGE,{"disambiguationData":[OSD([subQ0]),TDD([makeQuery(id+"F0.imprint","IMPRINT",EDGE,{"disambiguationData":[TD([[makeQuery(id+"F0.imprint","INTERSECT",VERTEX,{"derivedFrom":[subQ0,sQuery(id+"F0.wireOp",EDGE,"E25")]}),-1.0]])],"derivedFrom":subQ0})])],"isStart":false});}
            var Q1;
            Q1=makeQuery(id+"F2.opExtrude","CAP_EDGE",EDGE,{"disambiguationData":[OSD([sQuery(id+"F0.wireOp",EDGE,"E22")])],"isStart":false});
            var Q2;
            {var subQ0=sQuery(id+"F0.wireOp",EDGE,"E21");Q2=makeQuery(id+"F3.opExtrude","CAP_EDGE",EDGE,{"disambiguationData":[OSD([subQ0]),TDD([makeQuery(id+"F0.imprint","IMPRINT",EDGE,{"disambiguationData":[TD([[makeQuery(id+"F0.imprint","INTERSECT",VERTEX,{"derivedFrom":[subQ0,sQuery(id+"F0.wireOp",EDGE,"E29")]}),-1.0]])],"derivedFrom":subQ0})])],"isStart":false});}
            var Q3;
            {var subQ0=sQuery(id+"F0.wireOp",EDGE,"E21");Q3=makeQuery(id+"F3.opExtrude","CAP_EDGE",EDGE,{"disambiguationData":[OSD([subQ0]),TDD([makeQuery(id+"F0.imprint","IMPRINT",EDGE,{"disambiguationData":[TD([[makeQuery(id+"F0.imprint","INTERSECT",VERTEX,{"derivedFrom":[sQuery(id+"F0.wireOp",EDGE,"E18.top"),subQ0]}),-1.0]])],"derivedFrom":subQ0})])],"isStart":false});}
            var Q4;
            {var subQ0=sQuery(id+"F0.wireOp",EDGE,"E21");Q4=makeQuery(id+"F3.opExtrude","CAP_EDGE",EDGE,{"disambiguationData":[OSD([subQ0]),TDD([makeQuery(id+"F0.imprint","IMPRINT",EDGE,{"disambiguationData":[TD([[makeQuery(id+"F0.imprint","INTERSECT",VERTEX,{"derivedFrom":[sQuery(id+"F0.wireOp",EDGE,"E18.bottom"),subQ0]}),1.0]])],"derivedFrom":subQ0})])],"isStart":false});}
            fillet(context, id + "F14", {"entities" : qUnion([Q0, Q1, Q2, Q3, Q4]), "radius" : 6 * mm, "allowEdgeOverflow" : false});
        }
        {
            var Q0;
            {var subQ0=sQuery(id+"F0.wireOp",EDGE,"E28");var subQ1=sQuery(id+"F0.wireOp",EDGE,"E21");var subQ2=sQuery(id+"F0.wireOp",EDGE,"E19");var subQ3=sQuery(id+"F0.wireOp",EDGE,"E18.bottom");Q0=makeQuery(id+"F12.boolean.opBoolean","MERGE",FACE,{"derivedFrom":[makeQuery(id+"F11.opExtrude","SWEPT_FACE",FACE,{"disambiguationData":[OSD([subQ3,subQ2,subQ1,subQ0])]}),makeQuery(id+"F12.opExtrude","SWEPT_FACE",FACE,{"disambiguationData":[OSD([subQ3,subQ2,subQ1,subQ0])]})]});}
            var Q1;
            {var subQ0=sQuery(id+"F0.wireOp",EDGE,"E26");var subQ1=sQuery(id+"F0.wireOp",EDGE,"E25");var subQ2=sQuery(id+"F0.wireOp",EDGE,"E21");var subQ3=sQuery(id+"F0.wireOp",EDGE,"E19");Q1=makeQuery(id+"F12.boolean.opBoolean","MERGE",FACE,{"derivedFrom":[makeQuery(id+"F11.opExtrude","SWEPT_FACE",FACE,{"disambiguationData":[OSD([subQ3,subQ2,subQ1,subQ0])]}),makeQuery(id+"F12.opExtrude","SWEPT_FACE",FACE,{"disambiguationData":[OSD([subQ3,subQ2,subQ1,subQ0])]})]});}
            var Q2;
            {var subQ0=sQuery(id+"F0.wireOp",EDGE,"E29");var subQ1=sQuery(id+"F0.wireOp",EDGE,"E23");var subQ2=sQuery(id+"F0.wireOp",EDGE,"E21");var subQ3=sQuery(id+"F0.wireOp",EDGE,"E19");Q2=makeQuery(id+"F12.boolean.opBoolean","MERGE",FACE,{"derivedFrom":[makeQuery(id+"F11.opExtrude","SWEPT_FACE",FACE,{"disambiguationData":[OSD([subQ3,subQ2,subQ1,subQ0])]}),makeQuery(id+"F12.opExtrude","SWEPT_FACE",FACE,{"disambiguationData":[OSD([subQ3,subQ2,subQ1,subQ0])]})]});}
            var Q3;
            {var subQ0=sQuery(id+"F0.wireOp",EDGE,"E31");var subQ1=sQuery(id+"F0.wireOp",EDGE,"E21");var subQ2=sQuery(id+"F0.wireOp",EDGE,"E19");var subQ3=sQuery(id+"F0.wireOp",EDGE,"E18.top");Q3=makeQuery(id+"F12.boolean.opBoolean","MERGE",FACE,{"derivedFrom":[makeQuery(id+"F11.opExtrude","SWEPT_FACE",FACE,{"disambiguationData":[OSD([subQ3,subQ2,subQ1,subQ0])]}),makeQuery(id+"F12.opExtrude","SWEPT_FACE",FACE,{"disambiguationData":[OSD([subQ3,subQ2,subQ1,subQ0])]})]});}
            extrude(context, id + "F15", {"entities" : qUnion([Q0, Q1, Q2, Q3]), "operationType" : NewBodyOperationType.ADD, "depth" : 2 * mm});
        }
        {
            var Q0;
            {var subQ0=sQuery(id+"F0.wireOp",EDGE,"E19");var subQ1=sQuery(id+"F0.wireOp",EDGE,"E18.right");var subQ2=sQuery(id+"F0.wireOp",EDGE,"E18.top");var subQ3=sQuery(id+"F0.wireOp",EDGE,"E18.bottom");var subQ4=sQuery(id+"F0.wireOp",EDGE,"E26");var subQ5=sQuery(id+"F0.wireOp",EDGE,"E25");var subQ6=sQuery(id+"F0.wireOp",EDGE,"E21");var subQ7=sQuery(id+"F0.wireOp",EDGE,"E29");var subQ8=sQuery(id+"F0.wireOp",EDGE,"E23");var subQ9=sQuery(id+"F0.wireOp",EDGE,"E31");var subQ10=sQuery(id+"F0.wireOp",EDGE,"E28");var subQ11=sQuery(id+"F0.wireOp",EDGE,"E22");Q0=makeQuery(id+"F9.opChamfer","BLEND_EDGE",EDGE,{"disambiguationData":[OD(2.0)],"blendedFrom":[makeQuery(id+"F4.opExtrude","CAP_EDGE",EDGE,{"disambiguationData":[OSD([subQ1])],"isStart":true}),makeQuery(id+"F4.boolean.opBoolean","MERGE",FACE,{"derivedFrom":[makeQuery(id+"F3.boolean.opBoolean","MERGE",FACE,{"derivedFrom":[makeQuery(id+"F2.boolean.opBoolean","MERGE",FACE,{"derivedFrom":[makeQuery(id+"F1.opExtrude","CAP_FACE",FACE,{"disambiguationData":[OSD([sQuery(id+"F0.wireOp",EDGE,"E14"),sQuery(id+"F0.wireOp",EDGE,"E15"),sQuery(id+"F0.wireOp",EDGE,"E16"),sQuery(id+"F0.wireOp",EDGE,"E17"),subQ3,subQ2,sQuery(id+"F0.wireOp",EDGE,"E18.left"),subQ11,sQuery(id+"F0.wireOp",EDGE,"E34"),sQuery(id+"F0.wireOp",EDGE,"E35"),sQuery(id+"F0.wireOp",EDGE,"E36"),sQuery(id+"F0.wireOp",EDGE,"E37"),sQuery(id+"F0.wireOp",EDGE,"E38.bottom"),sQuery(id+"F0.wireOp",EDGE,"E38.top"),sQuery(id+"F0.wireOp",EDGE,"E38.left"),sQuery(id+"F0.wireOp",EDGE,"E38.right"),sQuery(id+"F0.wireOp",EDGE,"E39.bottom"),sQuery(id+"F0.wireOp",EDGE,"E39.top"),sQuery(id+"F0.wireOp",EDGE,"E39.left"),sQuery(id+"F0.wireOp",EDGE,"E39.right"),sQuery(id+"F0.wireOp",EDGE,"E40"),sQuery(id+"F0.wireOp",EDGE,"E41")])],"isStart":true}),makeQuery(id+"F2.opExtrude","CAP_FACE",FACE,{"disambiguationData":[OSD([subQ3,subQ2,subQ6,subQ11,subQ8,sQuery(id+"F0.wireOp",EDGE,"E24"),subQ5,subQ4,sQuery(id+"F0.wireOp",EDGE,"E27"),subQ10,subQ7,sQuery(id+"F0.wireOp",EDGE,"E30"),subQ9])],"isStart":true})]}),makeQuery(id+"F3.opExtrude","CAP_FACE",FACE,{"disambiguationData":[OSD([subQ3,subQ0,subQ6,subQ10])],"isStart":true}),makeQuery(id+"F3.opExtrude","CAP_FACE",FACE,{"disambiguationData":[OSD([subQ2,subQ0,subQ6,subQ9])],"isStart":true}),makeQuery(id+"F3.opExtrude","CAP_FACE",FACE,{"disambiguationData":[OSD([subQ0,subQ6,subQ8,subQ7])],"isStart":true}),makeQuery(id+"F3.opExtrude","CAP_FACE",FACE,{"disambiguationData":[OSD([subQ0,subQ6,subQ5,subQ4])],"isStart":true})]}),makeQuery(id+"F4.opExtrude","CAP_FACE",FACE,{"disambiguationData":[OSD([subQ3,subQ2,subQ1,subQ0])],"isStart":true})]})],"blendedInto":[makeQuery(id+"F4.boolean.opBoolean","MERGE",FACE,{"derivedFrom":[makeQuery(id+"F3.boolean.opBoolean","MERGE",FACE,{"derivedFrom":[makeQuery(id+"F2.boolean.opBoolean","MERGE",FACE,{"derivedFrom":[makeQuery(id+"F1.opExtrude","CAP_FACE",FACE,{"disambiguationData":[OSD([sQuery(id+"F0.wireOp",EDGE,"E14"),sQuery(id+"F0.wireOp",EDGE,"E15"),sQuery(id+"F0.wireOp",EDGE,"E16"),sQuery(id+"F0.wireOp",EDGE,"E17"),subQ3,subQ2,sQuery(id+"F0.wireOp",EDGE,"E18.left"),subQ11,sQuery(id+"F0.wireOp",EDGE,"E34"),sQuery(id+"F0.wireOp",EDGE,"E35"),sQuery(id+"F0.wireOp",EDGE,"E36"),sQuery(id+"F0.wireOp",EDGE,"E37"),sQuery(id+"F0.wireOp",EDGE,"E38.bottom"),sQuery(id+"F0.wireOp",EDGE,"E38.top"),sQuery(id+"F0.wireOp",EDGE,"E38.left"),sQuery(id+"F0.wireOp",EDGE,"E38.right"),sQuery(id+"F0.wireOp",EDGE,"E39.bottom"),sQuery(id+"F0.wireOp",EDGE,"E39.top"),sQuery(id+"F0.wireOp",EDGE,"E39.left"),sQuery(id+"F0.wireOp",EDGE,"E39.right"),sQuery(id+"F0.wireOp",EDGE,"E40"),sQuery(id+"F0.wireOp",EDGE,"E41")])],"isStart":true}),makeQuery(id+"F2.opExtrude","CAP_FACE",FACE,{"disambiguationData":[OSD([subQ3,subQ2,subQ6,subQ11,subQ8,sQuery(id+"F0.wireOp",EDGE,"E24"),subQ5,subQ4,sQuery(id+"F0.wireOp",EDGE,"E27"),subQ10,subQ7,sQuery(id+"F0.wireOp",EDGE,"E30"),subQ9])],"isStart":true})]}),makeQuery(id+"F3.opExtrude","CAP_FACE",FACE,{"disambiguationData":[OSD([subQ3,subQ0,subQ6,subQ10])],"isStart":true}),makeQuery(id+"F3.opExtrude","CAP_FACE",FACE,{"disambiguationData":[OSD([subQ2,subQ0,subQ6,subQ9])],"isStart":true}),makeQuery(id+"F3.opExtrude","CAP_FACE",FACE,{"disambiguationData":[OSD([subQ0,subQ6,subQ8,subQ7])],"isStart":true}),makeQuery(id+"F3.opExtrude","CAP_FACE",FACE,{"disambiguationData":[OSD([subQ0,subQ6,subQ5,subQ4])],"isStart":true})]}),makeQuery(id+"F4.opExtrude","CAP_FACE",FACE,{"disambiguationData":[OSD([subQ3,subQ2,subQ1,subQ0])],"isStart":true})]})]});}
            var Q1;
            {var subQ0=sQuery(id+"F0.wireOp",EDGE,"E19");var subQ1=sQuery(id+"F0.wireOp",EDGE,"E18.right");var subQ2=sQuery(id+"F0.wireOp",EDGE,"E18.top");var subQ3=sQuery(id+"F0.wireOp",EDGE,"E18.bottom");var subQ4=sQuery(id+"F0.wireOp",EDGE,"E26");var subQ5=sQuery(id+"F0.wireOp",EDGE,"E25");var subQ6=sQuery(id+"F0.wireOp",EDGE,"E21");var subQ7=sQuery(id+"F0.wireOp",EDGE,"E29");var subQ8=sQuery(id+"F0.wireOp",EDGE,"E23");var subQ9=sQuery(id+"F0.wireOp",EDGE,"E31");var subQ10=sQuery(id+"F0.wireOp",EDGE,"E28");var subQ11=sQuery(id+"F0.wireOp",EDGE,"E22");Q1=makeQuery(id+"F9.opChamfer","BLEND_EDGE",EDGE,{"disambiguationData":[OD(1.0)],"blendedFrom":[makeQuery(id+"F4.opExtrude","CAP_EDGE",EDGE,{"disambiguationData":[OSD([subQ1])],"isStart":true}),makeQuery(id+"F4.boolean.opBoolean","MERGE",FACE,{"derivedFrom":[makeQuery(id+"F3.boolean.opBoolean","MERGE",FACE,{"derivedFrom":[makeQuery(id+"F2.boolean.opBoolean","MERGE",FACE,{"derivedFrom":[makeQuery(id+"F1.opExtrude","CAP_FACE",FACE,{"disambiguationData":[OSD([sQuery(id+"F0.wireOp",EDGE,"E14"),sQuery(id+"F0.wireOp",EDGE,"E15"),sQuery(id+"F0.wireOp",EDGE,"E16"),sQuery(id+"F0.wireOp",EDGE,"E17"),subQ3,subQ2,sQuery(id+"F0.wireOp",EDGE,"E18.left"),subQ11,sQuery(id+"F0.wireOp",EDGE,"E34"),sQuery(id+"F0.wireOp",EDGE,"E35"),sQuery(id+"F0.wireOp",EDGE,"E36"),sQuery(id+"F0.wireOp",EDGE,"E37"),sQuery(id+"F0.wireOp",EDGE,"E38.bottom"),sQuery(id+"F0.wireOp",EDGE,"E38.top"),sQuery(id+"F0.wireOp",EDGE,"E38.left"),sQuery(id+"F0.wireOp",EDGE,"E38.right"),sQuery(id+"F0.wireOp",EDGE,"E39.bottom"),sQuery(id+"F0.wireOp",EDGE,"E39.top"),sQuery(id+"F0.wireOp",EDGE,"E39.left"),sQuery(id+"F0.wireOp",EDGE,"E39.right"),sQuery(id+"F0.wireOp",EDGE,"E40"),sQuery(id+"F0.wireOp",EDGE,"E41")])],"isStart":true}),makeQuery(id+"F2.opExtrude","CAP_FACE",FACE,{"disambiguationData":[OSD([subQ3,subQ2,subQ6,subQ11,subQ8,sQuery(id+"F0.wireOp",EDGE,"E24"),subQ5,subQ4,sQuery(id+"F0.wireOp",EDGE,"E27"),subQ10,subQ7,sQuery(id+"F0.wireOp",EDGE,"E30"),subQ9])],"isStart":true})]}),makeQuery(id+"F3.opExtrude","CAP_FACE",FACE,{"disambiguationData":[OSD([subQ3,subQ0,subQ6,subQ10])],"isStart":true}),makeQuery(id+"F3.opExtrude","CAP_FACE",FACE,{"disambiguationData":[OSD([subQ2,subQ0,subQ6,subQ9])],"isStart":true}),makeQuery(id+"F3.opExtrude","CAP_FACE",FACE,{"disambiguationData":[OSD([subQ0,subQ6,subQ8,subQ7])],"isStart":true}),makeQuery(id+"F3.opExtrude","CAP_FACE",FACE,{"disambiguationData":[OSD([subQ0,subQ6,subQ5,subQ4])],"isStart":true})]}),makeQuery(id+"F4.opExtrude","CAP_FACE",FACE,{"disambiguationData":[OSD([subQ3,subQ2,subQ1,subQ0])],"isStart":true})]})],"blendedInto":[makeQuery(id+"F4.boolean.opBoolean","MERGE",FACE,{"derivedFrom":[makeQuery(id+"F3.boolean.opBoolean","MERGE",FACE,{"derivedFrom":[makeQuery(id+"F2.boolean.opBoolean","MERGE",FACE,{"derivedFrom":[makeQuery(id+"F1.opExtrude","CAP_FACE",FACE,{"disambiguationData":[OSD([sQuery(id+"F0.wireOp",EDGE,"E14"),sQuery(id+"F0.wireOp",EDGE,"E15"),sQuery(id+"F0.wireOp",EDGE,"E16"),sQuery(id+"F0.wireOp",EDGE,"E17"),subQ3,subQ2,sQuery(id+"F0.wireOp",EDGE,"E18.left"),subQ11,sQuery(id+"F0.wireOp",EDGE,"E34"),sQuery(id+"F0.wireOp",EDGE,"E35"),sQuery(id+"F0.wireOp",EDGE,"E36"),sQuery(id+"F0.wireOp",EDGE,"E37"),sQuery(id+"F0.wireOp",EDGE,"E38.bottom"),sQuery(id+"F0.wireOp",EDGE,"E38.top"),sQuery(id+"F0.wireOp",EDGE,"E38.left"),sQuery(id+"F0.wireOp",EDGE,"E38.right"),sQuery(id+"F0.wireOp",EDGE,"E39.bottom"),sQuery(id+"F0.wireOp",EDGE,"E39.top"),sQuery(id+"F0.wireOp",EDGE,"E39.left"),sQuery(id+"F0.wireOp",EDGE,"E39.right"),sQuery(id+"F0.wireOp",EDGE,"E40"),sQuery(id+"F0.wireOp",EDGE,"E41")])],"isStart":true}),makeQuery(id+"F2.opExtrude","CAP_FACE",FACE,{"disambiguationData":[OSD([subQ3,subQ2,subQ6,subQ11,subQ8,sQuery(id+"F0.wireOp",EDGE,"E24"),subQ5,subQ4,sQuery(id+"F0.wireOp",EDGE,"E27"),subQ10,subQ7,sQuery(id+"F0.wireOp",EDGE,"E30"),subQ9])],"isStart":true})]}),makeQuery(id+"F3.opExtrude","CAP_FACE",FACE,{"disambiguationData":[OSD([subQ3,subQ0,subQ6,subQ10])],"isStart":true}),makeQuery(id+"F3.opExtrude","CAP_FACE",FACE,{"disambiguationData":[OSD([subQ2,subQ0,subQ6,subQ9])],"isStart":true}),makeQuery(id+"F3.opExtrude","CAP_FACE",FACE,{"disambiguationData":[OSD([subQ0,subQ6,subQ8,subQ7])],"isStart":true}),makeQuery(id+"F3.opExtrude","CAP_FACE",FACE,{"disambiguationData":[OSD([subQ0,subQ6,subQ5,subQ4])],"isStart":true})]}),makeQuery(id+"F4.opExtrude","CAP_FACE",FACE,{"disambiguationData":[OSD([subQ3,subQ2,subQ1,subQ0])],"isStart":true})]})]});}
            var Q2;
            {var subQ0=sQuery(id+"F0.wireOp",EDGE,"E19");var subQ1=sQuery(id+"F0.wireOp",EDGE,"E18.right");var subQ2=sQuery(id+"F0.wireOp",EDGE,"E18.top");var subQ3=sQuery(id+"F0.wireOp",EDGE,"E18.bottom");var subQ4=sQuery(id+"F0.wireOp",EDGE,"E26");var subQ5=sQuery(id+"F0.wireOp",EDGE,"E25");var subQ6=sQuery(id+"F0.wireOp",EDGE,"E21");var subQ7=sQuery(id+"F0.wireOp",EDGE,"E29");var subQ8=sQuery(id+"F0.wireOp",EDGE,"E23");var subQ9=sQuery(id+"F0.wireOp",EDGE,"E31");var subQ10=sQuery(id+"F0.wireOp",EDGE,"E28");var subQ11=sQuery(id+"F0.wireOp",EDGE,"E22");Q2=makeQuery(id+"F9.opChamfer","BLEND_EDGE",EDGE,{"disambiguationData":[OD(0.0)],"blendedFrom":[makeQuery(id+"F4.opExtrude","CAP_EDGE",EDGE,{"disambiguationData":[OSD([subQ1])],"isStart":true}),makeQuery(id+"F4.boolean.opBoolean","MERGE",FACE,{"derivedFrom":[makeQuery(id+"F3.boolean.opBoolean","MERGE",FACE,{"derivedFrom":[makeQuery(id+"F2.boolean.opBoolean","MERGE",FACE,{"derivedFrom":[makeQuery(id+"F1.opExtrude","CAP_FACE",FACE,{"disambiguationData":[OSD([sQuery(id+"F0.wireOp",EDGE,"E14"),sQuery(id+"F0.wireOp",EDGE,"E15"),sQuery(id+"F0.wireOp",EDGE,"E16"),sQuery(id+"F0.wireOp",EDGE,"E17"),subQ3,subQ2,sQuery(id+"F0.wireOp",EDGE,"E18.left"),subQ11,sQuery(id+"F0.wireOp",EDGE,"E34"),sQuery(id+"F0.wireOp",EDGE,"E35"),sQuery(id+"F0.wireOp",EDGE,"E36"),sQuery(id+"F0.wireOp",EDGE,"E37"),sQuery(id+"F0.wireOp",EDGE,"E38.bottom"),sQuery(id+"F0.wireOp",EDGE,"E38.top"),sQuery(id+"F0.wireOp",EDGE,"E38.left"),sQuery(id+"F0.wireOp",EDGE,"E38.right"),sQuery(id+"F0.wireOp",EDGE,"E39.bottom"),sQuery(id+"F0.wireOp",EDGE,"E39.top"),sQuery(id+"F0.wireOp",EDGE,"E39.left"),sQuery(id+"F0.wireOp",EDGE,"E39.right"),sQuery(id+"F0.wireOp",EDGE,"E40"),sQuery(id+"F0.wireOp",EDGE,"E41")])],"isStart":true}),makeQuery(id+"F2.opExtrude","CAP_FACE",FACE,{"disambiguationData":[OSD([subQ3,subQ2,subQ6,subQ11,subQ8,sQuery(id+"F0.wireOp",EDGE,"E24"),subQ5,subQ4,sQuery(id+"F0.wireOp",EDGE,"E27"),subQ10,subQ7,sQuery(id+"F0.wireOp",EDGE,"E30"),subQ9])],"isStart":true})]}),makeQuery(id+"F3.opExtrude","CAP_FACE",FACE,{"disambiguationData":[OSD([subQ3,subQ0,subQ6,subQ10])],"isStart":true}),makeQuery(id+"F3.opExtrude","CAP_FACE",FACE,{"disambiguationData":[OSD([subQ2,subQ0,subQ6,subQ9])],"isStart":true}),makeQuery(id+"F3.opExtrude","CAP_FACE",FACE,{"disambiguationData":[OSD([subQ0,subQ6,subQ8,subQ7])],"isStart":true}),makeQuery(id+"F3.opExtrude","CAP_FACE",FACE,{"disambiguationData":[OSD([subQ0,subQ6,subQ5,subQ4])],"isStart":true})]}),makeQuery(id+"F4.opExtrude","CAP_FACE",FACE,{"disambiguationData":[OSD([subQ3,subQ2,subQ1,subQ0])],"isStart":true})]})],"blendedInto":[makeQuery(id+"F4.boolean.opBoolean","MERGE",FACE,{"derivedFrom":[makeQuery(id+"F3.boolean.opBoolean","MERGE",FACE,{"derivedFrom":[makeQuery(id+"F2.boolean.opBoolean","MERGE",FACE,{"derivedFrom":[makeQuery(id+"F1.opExtrude","CAP_FACE",FACE,{"disambiguationData":[OSD([sQuery(id+"F0.wireOp",EDGE,"E14"),sQuery(id+"F0.wireOp",EDGE,"E15"),sQuery(id+"F0.wireOp",EDGE,"E16"),sQuery(id+"F0.wireOp",EDGE,"E17"),subQ3,subQ2,sQuery(id+"F0.wireOp",EDGE,"E18.left"),subQ11,sQuery(id+"F0.wireOp",EDGE,"E34"),sQuery(id+"F0.wireOp",EDGE,"E35"),sQuery(id+"F0.wireOp",EDGE,"E36"),sQuery(id+"F0.wireOp",EDGE,"E37"),sQuery(id+"F0.wireOp",EDGE,"E38.bottom"),sQuery(id+"F0.wireOp",EDGE,"E38.top"),sQuery(id+"F0.wireOp",EDGE,"E38.left"),sQuery(id+"F0.wireOp",EDGE,"E38.right"),sQuery(id+"F0.wireOp",EDGE,"E39.bottom"),sQuery(id+"F0.wireOp",EDGE,"E39.top"),sQuery(id+"F0.wireOp",EDGE,"E39.left"),sQuery(id+"F0.wireOp",EDGE,"E39.right"),sQuery(id+"F0.wireOp",EDGE,"E40"),sQuery(id+"F0.wireOp",EDGE,"E41")])],"isStart":true}),makeQuery(id+"F2.opExtrude","CAP_FACE",FACE,{"disambiguationData":[OSD([subQ3,subQ2,subQ6,subQ11,subQ8,sQuery(id+"F0.wireOp",EDGE,"E24"),subQ5,subQ4,sQuery(id+"F0.wireOp",EDGE,"E27"),subQ10,subQ7,sQuery(id+"F0.wireOp",EDGE,"E30"),subQ9])],"isStart":true})]}),makeQuery(id+"F3.opExtrude","CAP_FACE",FACE,{"disambiguationData":[OSD([subQ3,subQ0,subQ6,subQ10])],"isStart":true}),makeQuery(id+"F3.opExtrude","CAP_FACE",FACE,{"disambiguationData":[OSD([subQ2,subQ0,subQ6,subQ9])],"isStart":true}),makeQuery(id+"F3.opExtrude","CAP_FACE",FACE,{"disambiguationData":[OSD([subQ0,subQ6,subQ8,subQ7])],"isStart":true}),makeQuery(id+"F3.opExtrude","CAP_FACE",FACE,{"disambiguationData":[OSD([subQ0,subQ6,subQ5,subQ4])],"isStart":true})]}),makeQuery(id+"F4.opExtrude","CAP_FACE",FACE,{"disambiguationData":[OSD([subQ3,subQ2,subQ1,subQ0])],"isStart":true})]})]});}
            var Q3;
            {var subQ0=sQuery(id+"F0.wireOp",EDGE,"E19");var subQ1=sQuery(id+"F0.wireOp",EDGE,"E18.right");var subQ2=sQuery(id+"F0.wireOp",EDGE,"E18.top");var subQ3=sQuery(id+"F0.wireOp",EDGE,"E18.bottom");var subQ4=sQuery(id+"F0.wireOp",EDGE,"E26");var subQ5=sQuery(id+"F0.wireOp",EDGE,"E25");var subQ6=sQuery(id+"F0.wireOp",EDGE,"E21");var subQ7=sQuery(id+"F0.wireOp",EDGE,"E29");var subQ8=sQuery(id+"F0.wireOp",EDGE,"E23");var subQ9=sQuery(id+"F0.wireOp",EDGE,"E31");var subQ10=sQuery(id+"F0.wireOp",EDGE,"E28");var subQ11=sQuery(id+"F0.wireOp",EDGE,"E22");Q3=makeQuery(id+"F9.opChamfer","BLEND_EDGE",EDGE,{"disambiguationData":[OD(3.0)],"blendedFrom":[makeQuery(id+"F4.opExtrude","CAP_EDGE",EDGE,{"disambiguationData":[OSD([subQ1])],"isStart":true}),makeQuery(id+"F4.boolean.opBoolean","MERGE",FACE,{"derivedFrom":[makeQuery(id+"F3.boolean.opBoolean","MERGE",FACE,{"derivedFrom":[makeQuery(id+"F2.boolean.opBoolean","MERGE",FACE,{"derivedFrom":[makeQuery(id+"F1.opExtrude","CAP_FACE",FACE,{"disambiguationData":[OSD([sQuery(id+"F0.wireOp",EDGE,"E14"),sQuery(id+"F0.wireOp",EDGE,"E15"),sQuery(id+"F0.wireOp",EDGE,"E16"),sQuery(id+"F0.wireOp",EDGE,"E17"),subQ3,subQ2,sQuery(id+"F0.wireOp",EDGE,"E18.left"),subQ11,sQuery(id+"F0.wireOp",EDGE,"E34"),sQuery(id+"F0.wireOp",EDGE,"E35"),sQuery(id+"F0.wireOp",EDGE,"E36"),sQuery(id+"F0.wireOp",EDGE,"E37"),sQuery(id+"F0.wireOp",EDGE,"E38.bottom"),sQuery(id+"F0.wireOp",EDGE,"E38.top"),sQuery(id+"F0.wireOp",EDGE,"E38.left"),sQuery(id+"F0.wireOp",EDGE,"E38.right"),sQuery(id+"F0.wireOp",EDGE,"E39.bottom"),sQuery(id+"F0.wireOp",EDGE,"E39.top"),sQuery(id+"F0.wireOp",EDGE,"E39.left"),sQuery(id+"F0.wireOp",EDGE,"E39.right"),sQuery(id+"F0.wireOp",EDGE,"E40"),sQuery(id+"F0.wireOp",EDGE,"E41")])],"isStart":true}),makeQuery(id+"F2.opExtrude","CAP_FACE",FACE,{"disambiguationData":[OSD([subQ3,subQ2,subQ6,subQ11,subQ8,sQuery(id+"F0.wireOp",EDGE,"E24"),subQ5,subQ4,sQuery(id+"F0.wireOp",EDGE,"E27"),subQ10,subQ7,sQuery(id+"F0.wireOp",EDGE,"E30"),subQ9])],"isStart":true})]}),makeQuery(id+"F3.opExtrude","CAP_FACE",FACE,{"disambiguationData":[OSD([subQ3,subQ0,subQ6,subQ10])],"isStart":true}),makeQuery(id+"F3.opExtrude","CAP_FACE",FACE,{"disambiguationData":[OSD([subQ2,subQ0,subQ6,subQ9])],"isStart":true}),makeQuery(id+"F3.opExtrude","CAP_FACE",FACE,{"disambiguationData":[OSD([subQ0,subQ6,subQ8,subQ7])],"isStart":true}),makeQuery(id+"F3.opExtrude","CAP_FACE",FACE,{"disambiguationData":[OSD([subQ0,subQ6,subQ5,subQ4])],"isStart":true})]}),makeQuery(id+"F4.opExtrude","CAP_FACE",FACE,{"disambiguationData":[OSD([subQ3,subQ2,subQ1,subQ0])],"isStart":true})]})],"blendedInto":[makeQuery(id+"F4.boolean.opBoolean","MERGE",FACE,{"derivedFrom":[makeQuery(id+"F3.boolean.opBoolean","MERGE",FACE,{"derivedFrom":[makeQuery(id+"F2.boolean.opBoolean","MERGE",FACE,{"derivedFrom":[makeQuery(id+"F1.opExtrude","CAP_FACE",FACE,{"disambiguationData":[OSD([sQuery(id+"F0.wireOp",EDGE,"E14"),sQuery(id+"F0.wireOp",EDGE,"E15"),sQuery(id+"F0.wireOp",EDGE,"E16"),sQuery(id+"F0.wireOp",EDGE,"E17"),subQ3,subQ2,sQuery(id+"F0.wireOp",EDGE,"E18.left"),subQ11,sQuery(id+"F0.wireOp",EDGE,"E34"),sQuery(id+"F0.wireOp",EDGE,"E35"),sQuery(id+"F0.wireOp",EDGE,"E36"),sQuery(id+"F0.wireOp",EDGE,"E37"),sQuery(id+"F0.wireOp",EDGE,"E38.bottom"),sQuery(id+"F0.wireOp",EDGE,"E38.top"),sQuery(id+"F0.wireOp",EDGE,"E38.left"),sQuery(id+"F0.wireOp",EDGE,"E38.right"),sQuery(id+"F0.wireOp",EDGE,"E39.bottom"),sQuery(id+"F0.wireOp",EDGE,"E39.top"),sQuery(id+"F0.wireOp",EDGE,"E39.left"),sQuery(id+"F0.wireOp",EDGE,"E39.right"),sQuery(id+"F0.wireOp",EDGE,"E40"),sQuery(id+"F0.wireOp",EDGE,"E41")])],"isStart":true}),makeQuery(id+"F2.opExtrude","CAP_FACE",FACE,{"disambiguationData":[OSD([subQ3,subQ2,subQ6,subQ11,subQ8,sQuery(id+"F0.wireOp",EDGE,"E24"),subQ5,subQ4,sQuery(id+"F0.wireOp",EDGE,"E27"),subQ10,subQ7,sQuery(id+"F0.wireOp",EDGE,"E30"),subQ9])],"isStart":true})]}),makeQuery(id+"F3.opExtrude","CAP_FACE",FACE,{"disambiguationData":[OSD([subQ3,subQ0,subQ6,subQ10])],"isStart":true}),makeQuery(id+"F3.opExtrude","CAP_FACE",FACE,{"disambiguationData":[OSD([subQ2,subQ0,subQ6,subQ9])],"isStart":true}),makeQuery(id+"F3.opExtrude","CAP_FACE",FACE,{"disambiguationData":[OSD([subQ0,subQ6,subQ8,subQ7])],"isStart":true}),makeQuery(id+"F3.opExtrude","CAP_FACE",FACE,{"disambiguationData":[OSD([subQ0,subQ6,subQ5,subQ4])],"isStart":true})]}),makeQuery(id+"F4.opExtrude","CAP_FACE",FACE,{"disambiguationData":[OSD([subQ3,subQ2,subQ1,subQ0])],"isStart":true})]})]});}
            fillet(context, id + "F16", {"entities" : qUnion([Q0, Q1, Q2, Q3]), "radius" : 5 * mm, "tangentPropagation" : true, "allowEdgeOverflow" : false});
        }
        {
            var Q0;
            {var subQ0=sQuery(id+"F0.wireOp",EDGE,"E28");var subQ1=sQuery(id+"F0.wireOp",EDGE,"E21");var subQ2=sQuery(id+"F0.wireOp",EDGE,"E19");var subQ3=sQuery(id+"F0.wireOp",EDGE,"E18.bottom");Q0=makeQuery(id+"F15.opExtrude","CAP_EDGE",EDGE,{"disambiguationData":[OSD([subQ3,subQ2,subQ1,subQ0]),TDD([makeQuery(id+"F11.boolean.opBoolean","MERGE",EDGE,{"derivedFrom":[makeQuery(id+"F10.opChamfer","BLEND_EDGE",EDGE,{"blendedFrom":[makeQuery(id+"F3.opExtrude","CAP_EDGE",EDGE,{"disambiguationData":[OSD([subQ2]),TDD([makeQuery(id+"F0.imprint","IMPRINT",EDGE,{"disambiguationData":[TD([[makeQuery(id+"F0.imprint","INTERSECT",VERTEX,{"derivedFrom":[subQ3,subQ2]}),1.0]])],"derivedFrom":subQ2})])],"isStart":false}),makeQuery(id+"F3.opExtrude","CAP_FACE",FACE,{"disambiguationData":[OSD([subQ3,subQ2,subQ1,subQ0])],"isStart":false})],"blendedInto":[makeQuery(id+"F3.opExtrude","CAP_FACE",FACE,{"disambiguationData":[OSD([subQ3,subQ2,subQ1,subQ0])],"isStart":false})]}),makeQuery(id+"F11.opExtrude","CAP_EDGE",EDGE,{"disambiguationData":[OSD([subQ3,subQ2,subQ1,subQ0])],"isStart":true})]})])],"isStart":false});}
            var Q1;
            {var subQ0=sQuery(id+"F0.wireOp",EDGE,"E26");var subQ1=sQuery(id+"F0.wireOp",EDGE,"E25");var subQ2=sQuery(id+"F0.wireOp",EDGE,"E21");var subQ3=sQuery(id+"F0.wireOp",EDGE,"E19");Q1=makeQuery(id+"F15.opExtrude","CAP_EDGE",EDGE,{"disambiguationData":[OSD([subQ3,subQ2,subQ1,subQ0]),TDD([makeQuery(id+"F11.boolean.opBoolean","MERGE",EDGE,{"derivedFrom":[makeQuery(id+"F10.opChamfer","BLEND_EDGE",EDGE,{"blendedFrom":[makeQuery(id+"F3.opExtrude","CAP_EDGE",EDGE,{"disambiguationData":[OSD([subQ3]),TDD([makeQuery(id+"F0.imprint","IMPRINT",EDGE,{"disambiguationData":[TD([[makeQuery(id+"F0.imprint","INTERSECT",VERTEX,{"derivedFrom":[subQ3,subQ1]}),-1.0]])],"derivedFrom":subQ3})])],"isStart":false}),makeQuery(id+"F3.opExtrude","CAP_FACE",FACE,{"disambiguationData":[OSD([subQ3,subQ2,subQ1,subQ0])],"isStart":false})],"blendedInto":[makeQuery(id+"F3.opExtrude","CAP_FACE",FACE,{"disambiguationData":[OSD([subQ3,subQ2,subQ1,subQ0])],"isStart":false})]}),makeQuery(id+"F11.opExtrude","CAP_EDGE",EDGE,{"disambiguationData":[OSD([subQ3,subQ2,subQ1,subQ0])],"isStart":true})]})])],"isStart":false});}
            var Q2;
            {var subQ0=sQuery(id+"F0.wireOp",EDGE,"E29");var subQ1=sQuery(id+"F0.wireOp",EDGE,"E23");var subQ2=sQuery(id+"F0.wireOp",EDGE,"E21");var subQ3=sQuery(id+"F0.wireOp",EDGE,"E19");Q2=makeQuery(id+"F15.opExtrude","CAP_EDGE",EDGE,{"disambiguationData":[OSD([subQ3,subQ2,subQ1,subQ0]),TDD([makeQuery(id+"F11.boolean.opBoolean","MERGE",EDGE,{"derivedFrom":[makeQuery(id+"F10.opChamfer","BLEND_EDGE",EDGE,{"blendedFrom":[makeQuery(id+"F3.opExtrude","CAP_EDGE",EDGE,{"disambiguationData":[OSD([subQ3]),TDD([makeQuery(id+"F0.imprint","IMPRINT",EDGE,{"disambiguationData":[TD([[makeQuery(id+"F0.imprint","INTERSECT",VERTEX,{"derivedFrom":[subQ3,subQ0]}),-1.0]])],"derivedFrom":subQ3})])],"isStart":false}),makeQuery(id+"F3.opExtrude","CAP_FACE",FACE,{"disambiguationData":[OSD([subQ3,subQ2,subQ1,subQ0])],"isStart":false})],"blendedInto":[makeQuery(id+"F3.opExtrude","CAP_FACE",FACE,{"disambiguationData":[OSD([subQ3,subQ2,subQ1,subQ0])],"isStart":false})]}),makeQuery(id+"F11.opExtrude","CAP_EDGE",EDGE,{"disambiguationData":[OSD([subQ3,subQ2,subQ1,subQ0])],"isStart":true})]})])],"isStart":false});}
            var Q3;
            {var subQ0=sQuery(id+"F0.wireOp",EDGE,"E31");var subQ1=sQuery(id+"F0.wireOp",EDGE,"E21");var subQ2=sQuery(id+"F0.wireOp",EDGE,"E19");var subQ3=sQuery(id+"F0.wireOp",EDGE,"E18.top");Q3=makeQuery(id+"F15.opExtrude","CAP_EDGE",EDGE,{"disambiguationData":[OSD([subQ3,subQ2,subQ1,subQ0]),TDD([makeQuery(id+"F11.boolean.opBoolean","MERGE",EDGE,{"derivedFrom":[makeQuery(id+"F10.opChamfer","BLEND_EDGE",EDGE,{"blendedFrom":[makeQuery(id+"F3.opExtrude","CAP_EDGE",EDGE,{"disambiguationData":[OSD([subQ2]),TDD([makeQuery(id+"F0.imprint","IMPRINT",EDGE,{"disambiguationData":[TD([[makeQuery(id+"F0.imprint","INTERSECT",VERTEX,{"derivedFrom":[subQ3,subQ2]}),-1.0]])],"derivedFrom":subQ2})])],"isStart":false}),makeQuery(id+"F3.opExtrude","CAP_FACE",FACE,{"disambiguationData":[OSD([subQ3,subQ2,subQ1,subQ0])],"isStart":false})],"blendedInto":[makeQuery(id+"F3.opExtrude","CAP_FACE",FACE,{"disambiguationData":[OSD([subQ3,subQ2,subQ1,subQ0])],"isStart":false})]}),makeQuery(id+"F11.opExtrude","CAP_EDGE",EDGE,{"disambiguationData":[OSD([subQ3,subQ2,subQ1,subQ0])],"isStart":true})]})])],"isStart":false});}
            chamfer(context, id + "F17", {"entities" : qUnion([Q0, Q1, Q2, Q3]), "chamferType" : ChamferType.TWO_OFFSETS, "width1" : 2 * mm, "oppositeDirection" : false, "width2" : 10 * mm, "tangentPropagation" : true});
        }
        {
            var Q0;
            {var subQ0=sQuery(id+"F0.wireOp",EDGE,"E18.bottom");var subQ2=sQuery(id+"F0.wireOp",EDGE,"E19");var subQ3=makeQuery(id+"F0.imprint","IMPRINT",EDGE,{"disambiguationData":[TD([[makeQuery(id+"F0.imprint","INTERSECT",VERTEX,{"derivedFrom":[subQ0,subQ2]}),1.0]])],"derivedFrom":subQ2});var subQ4=sQuery(id+"F5.wireOp",EDGE,"E42.top");Q0=makeQuery(id+"F13.opChamfer","BLEND_FACE",FACE,{"disambiguationData":[OSD([subQ2,subQ4]),TDD([makeQuery(id+"F12.opExtrude","CAP_EDGE",EDGE,{"disambiguationData":[OSD([subQ2,subQ4]),TDD([makeQuery(id+"F11.opExtrude","CAP_EDGE",EDGE,{"disambiguationData":[OSD([subQ2,subQ4]),TDD([makeQuery(id+"F10.opChamfer","BLEND_EDGE",EDGE,{"blendedFrom":[makeQuery(id+"F3.opExtrude","CAP_EDGE",EDGE,{"disambiguationData":[OSD([subQ2]),TDD([subQ3])],"isStart":false}),makeQuery(id+"F6.boolean.opBoolean","COPY",FACE,{"disambiguationData":[TD([makeQuery(id+"F2.opExtrude","SWEPT_FACE",FACE,{"disambiguationData":[OSD([subQ0])]})])],"derivedFrom":makeQuery(id+"F6.opExtrude","SWEPT_FACE",FACE,{"disambiguationData":[OSD([subQ4])]})})],"blendedInto":[makeQuery(id+"F6.boolean.opBoolean","COPY",FACE,{"disambiguationData":[TD([makeQuery(id+"F2.opExtrude","SWEPT_FACE",FACE,{"disambiguationData":[OSD([subQ0])]})])],"derivedFrom":makeQuery(id+"F6.opExtrude","SWEPT_FACE",FACE,{"disambiguationData":[OSD([subQ4])]})})]})])],"isStart":false})])],"isStart":false})])]});}
            var Q1;
            {var subQ0=sQuery(id+"F0.wireOp",EDGE,"E25");var subQ1=sQuery(id+"F0.wireOp",EDGE,"E19");var subQ3=makeQuery(id+"F0.imprint","IMPRINT",EDGE,{"disambiguationData":[TD([[makeQuery(id+"F0.imprint","INTERSECT",VERTEX,{"derivedFrom":[subQ1,subQ0]}),-1.0]])],"derivedFrom":subQ1});var subQ4=sQuery(id+"F5.wireOp",EDGE,"E42.top");Q1=makeQuery(id+"F13.opChamfer","BLEND_FACE",FACE,{"disambiguationData":[OSD([subQ1,subQ4]),TDD([makeQuery(id+"F12.opExtrude","CAP_EDGE",EDGE,{"disambiguationData":[OSD([subQ1,subQ4]),TDD([makeQuery(id+"F11.opExtrude","CAP_EDGE",EDGE,{"disambiguationData":[OSD([subQ1,subQ4]),TDD([makeQuery(id+"F10.opChamfer","BLEND_EDGE",EDGE,{"blendedFrom":[makeQuery(id+"F3.opExtrude","CAP_EDGE",EDGE,{"disambiguationData":[OSD([subQ1]),TDD([subQ3])],"isStart":false}),makeQuery(id+"F6.boolean.opBoolean","COPY",FACE,{"disambiguationData":[TD([makeQuery(id+"F2.opExtrude","SWEPT_FACE",FACE,{"disambiguationData":[OSD([subQ0])]})])],"derivedFrom":makeQuery(id+"F6.opExtrude","SWEPT_FACE",FACE,{"disambiguationData":[OSD([subQ4])]})})],"blendedInto":[makeQuery(id+"F6.boolean.opBoolean","COPY",FACE,{"disambiguationData":[TD([makeQuery(id+"F2.opExtrude","SWEPT_FACE",FACE,{"disambiguationData":[OSD([subQ0])]})])],"derivedFrom":makeQuery(id+"F6.opExtrude","SWEPT_FACE",FACE,{"disambiguationData":[OSD([subQ4])]})})]})])],"isStart":false})])],"isStart":false})])]});}
            extrude(context, id + "F18", {"entities" : qUnion([Q0, Q1]), "operationType" : NewBodyOperationType.ADD, "oppositeDirection" : true, "depth" : 1 * mm});
        }
        {
            var Q0;
            {var subQ0=sQuery(id+"F0.wireOp",EDGE,"E19");var subQ1=sQuery(id+"F0.wireOp",EDGE,"E18.bottom");var subQ3=makeQuery(id+"F0.imprint","IMPRINT",EDGE,{"disambiguationData":[TD([[makeQuery(id+"F0.imprint","INTERSECT",VERTEX,{"derivedFrom":[subQ1,subQ0]}),1.0]])],"derivedFrom":subQ0});var subQ4=makeQuery(id+"F3.opExtrude","CAP_EDGE",EDGE,{"disambiguationData":[OSD([subQ0]),TDD([subQ3])],"isStart":false});var subQ5=sQuery(id+"F5.wireOp",EDGE,"E42.top");Q0=makeQuery(id+"F13.opChamfer","BLEND_EDGE",EDGE,{"blendedFrom":[makeQuery(id+"F12.opExtrude","CAP_EDGE",EDGE,{"disambiguationData":[OSD([subQ0,subQ5]),TDD([makeQuery(id+"F11.opExtrude","CAP_EDGE",EDGE,{"disambiguationData":[OSD([subQ0,subQ5]),TDD([makeQuery(id+"F10.opChamfer","BLEND_EDGE",EDGE,{"blendedFrom":[subQ4,makeQuery(id+"F6.boolean.opBoolean","COPY",FACE,{"disambiguationData":[TD([makeQuery(id+"F2.opExtrude","SWEPT_FACE",FACE,{"disambiguationData":[OSD([subQ1])]})])],"derivedFrom":makeQuery(id+"F6.opExtrude","SWEPT_FACE",FACE,{"disambiguationData":[OSD([subQ5])]})})],"blendedInto":[makeQuery(id+"F6.boolean.opBoolean","COPY",FACE,{"disambiguationData":[TD([makeQuery(id+"F2.opExtrude","SWEPT_FACE",FACE,{"disambiguationData":[OSD([subQ1])]})])],"derivedFrom":makeQuery(id+"F6.opExtrude","SWEPT_FACE",FACE,{"disambiguationData":[OSD([subQ5])]})})]})])],"isStart":false})])],"isStart":false}),makeQuery(id+"F12.opExtrude","CAP_FACE",FACE,{"disambiguationData":[OSD([subQ0]),TDD([makeQuery(id+"F11.opExtrude","CAP_FACE",FACE,{"disambiguationData":[OSD([subQ0]),TDD([makeQuery(id+"F10.opChamfer","BLEND_FACE",FACE,{"disambiguationData":[OSD([subQ0]),TDD([subQ4])]})])],"isStart":false})])],"isStart":false})],"blendedInto":[makeQuery(id+"F12.opExtrude","CAP_FACE",FACE,{"disambiguationData":[OSD([subQ0]),TDD([makeQuery(id+"F11.opExtrude","CAP_FACE",FACE,{"disambiguationData":[OSD([subQ0]),TDD([makeQuery(id+"F10.opChamfer","BLEND_FACE",FACE,{"disambiguationData":[OSD([subQ0]),TDD([subQ4])]})])],"isStart":false})])],"isStart":false})]});}
            var Q1;
            {var subQ0=sQuery(id+"F0.wireOp",EDGE,"E25");var subQ1=sQuery(id+"F0.wireOp",EDGE,"E19");var subQ3=makeQuery(id+"F0.imprint","IMPRINT",EDGE,{"disambiguationData":[TD([[makeQuery(id+"F0.imprint","INTERSECT",VERTEX,{"derivedFrom":[subQ1,subQ0]}),-1.0]])],"derivedFrom":subQ1});var subQ4=makeQuery(id+"F3.opExtrude","CAP_EDGE",EDGE,{"disambiguationData":[OSD([subQ1]),TDD([subQ3])],"isStart":false});var subQ5=sQuery(id+"F5.wireOp",EDGE,"E42.top");Q1=makeQuery(id+"F13.opChamfer","BLEND_EDGE",EDGE,{"blendedFrom":[makeQuery(id+"F12.opExtrude","CAP_EDGE",EDGE,{"disambiguationData":[OSD([subQ1,subQ5]),TDD([makeQuery(id+"F11.opExtrude","CAP_EDGE",EDGE,{"disambiguationData":[OSD([subQ1,subQ5]),TDD([makeQuery(id+"F10.opChamfer","BLEND_EDGE",EDGE,{"blendedFrom":[subQ4,makeQuery(id+"F6.boolean.opBoolean","COPY",FACE,{"disambiguationData":[TD([makeQuery(id+"F2.opExtrude","SWEPT_FACE",FACE,{"disambiguationData":[OSD([subQ0])]})])],"derivedFrom":makeQuery(id+"F6.opExtrude","SWEPT_FACE",FACE,{"disambiguationData":[OSD([subQ5])]})})],"blendedInto":[makeQuery(id+"F6.boolean.opBoolean","COPY",FACE,{"disambiguationData":[TD([makeQuery(id+"F2.opExtrude","SWEPT_FACE",FACE,{"disambiguationData":[OSD([subQ0])]})])],"derivedFrom":makeQuery(id+"F6.opExtrude","SWEPT_FACE",FACE,{"disambiguationData":[OSD([subQ5])]})})]})])],"isStart":false})])],"isStart":false}),makeQuery(id+"F12.opExtrude","CAP_FACE",FACE,{"disambiguationData":[OSD([subQ1]),TDD([makeQuery(id+"F11.opExtrude","CAP_FACE",FACE,{"disambiguationData":[OSD([subQ1]),TDD([makeQuery(id+"F10.opChamfer","BLEND_FACE",FACE,{"disambiguationData":[OSD([subQ1]),TDD([subQ4])]})])],"isStart":false})])],"isStart":false})],"blendedInto":[makeQuery(id+"F12.opExtrude","CAP_FACE",FACE,{"disambiguationData":[OSD([subQ1]),TDD([makeQuery(id+"F11.opExtrude","CAP_FACE",FACE,{"disambiguationData":[OSD([subQ1]),TDD([makeQuery(id+"F10.opChamfer","BLEND_FACE",FACE,{"disambiguationData":[OSD([subQ1]),TDD([subQ4])]})])],"isStart":false})])],"isStart":false})]});}
            var Q2;
            Q2=makeQuery(id+"F4.opExtrude","CAP_EDGE",EDGE,{"disambiguationData":[OSD([sQuery(id+"F0.wireOp",EDGE,"E18.right")])],"isStart":false});
            var Q3;
            {var subQ0=sQuery(id+"F0.wireOp",EDGE,"E18.right");Q3=makeQuery(id+"F9.opChamfer","BLEND_EDGE",EDGE,{"blendedFrom":[makeQuery(id+"F4.opExtrude","CAP_EDGE",EDGE,{"disambiguationData":[OSD([subQ0])],"isStart":true}),makeQuery(id+"F4.opExtrude","SWEPT_FACE",FACE,{"disambiguationData":[OSD([subQ0])]})],"blendedInto":[makeQuery(id+"F4.opExtrude","SWEPT_FACE",FACE,{"disambiguationData":[OSD([subQ0])]})]});}
            fillet(context, id + "F19", {"entities" : qUnion([Q0, Q1, Q2, Q3]), "radius" : 1 * mm, "tangentPropagation" : true, "allowEdgeOverflow" : false});
        }
        {
            var Q0;
            {var subQ0=sQuery(id+"F0.wireOp",EDGE,"E28");var subQ1=sQuery(id+"F0.wireOp",EDGE,"E21");var subQ2=sQuery(id+"F0.wireOp",EDGE,"E19");var subQ3=sQuery(id+"F0.wireOp",EDGE,"E18.bottom");var subQ4=makeQuery(id+"F10.opChamfer","BLEND_VERTEX",VERTEX,{"blendedFrom":[makeQuery(id+"F3.opExtrude","CAP_EDGE",EDGE,{"disambiguationData":[OSD([subQ2]),TDD([makeQuery(id+"F0.imprint","IMPRINT",EDGE,{"disambiguationData":[TD([[makeQuery(id+"F0.imprint","INTERSECT",VERTEX,{"derivedFrom":[subQ3,subQ2]}),1.0]])],"derivedFrom":subQ2})])],"isStart":false}),makeQuery(id+"F3.opExtrude","CAP_FACE",FACE,{"disambiguationData":[OSD([subQ3,subQ2,subQ1,subQ0])],"isStart":false}),makeQuery(id+"F3.boolean.opBoolean","MERGE",FACE,{"derivedFrom":[makeQuery(id+"F2.opExtrude","SWEPT_FACE",FACE,{"disambiguationData":[OSD([subQ0])]}),makeQuery(id+"F3.opExtrude","SWEPT_FACE",FACE,{"disambiguationData":[OSD([subQ0])]})]})],"blendedInto":[makeQuery(id+"F3.opExtrude","CAP_FACE",FACE,{"disambiguationData":[OSD([subQ3,subQ2,subQ1,subQ0])],"isStart":false}),makeQuery(id+"F3.boolean.opBoolean","MERGE",FACE,{"derivedFrom":[makeQuery(id+"F2.opExtrude","SWEPT_FACE",FACE,{"disambiguationData":[OSD([subQ0])]}),makeQuery(id+"F3.opExtrude","SWEPT_FACE",FACE,{"disambiguationData":[OSD([subQ0])]})]})]});Q0=makeQuery(id+"F15.opExtrude","CAP_EDGE",EDGE,{"disambiguationData":[OSD([subQ3,subQ2,subQ1,subQ0]),TDD([makeQuery(id+"F12.boolean.opBoolean","MERGE",EDGE,{"derivedFrom":[makeQuery(id+"F11.opExtrude","SWEPT_EDGE",EDGE,{"disambiguationData":[OSD([subQ3,subQ2,subQ1,subQ0]),TDD([subQ4])]}),makeQuery(id+"F12.opExtrude","SWEPT_EDGE",EDGE,{"disambiguationData":[OSD([subQ3,subQ2,subQ1,subQ0]),TDD([makeQuery(id+"F11.opExtrude","CAP_VERTEX",VERTEX,{"disambiguationData":[OSD([subQ3,subQ2,subQ1,subQ0]),TDD([subQ4])],"isStart":false})])]})]})])],"isStart":false});}
            var Q1;
            {var subQ0=sQuery(id+"F0.wireOp",EDGE,"E26");var subQ1=sQuery(id+"F0.wireOp",EDGE,"E25");var subQ2=sQuery(id+"F0.wireOp",EDGE,"E21");var subQ3=sQuery(id+"F0.wireOp",EDGE,"E19");var subQ4=makeQuery(id+"F10.opChamfer","BLEND_VERTEX",VERTEX,{"blendedFrom":[makeQuery(id+"F3.opExtrude","CAP_EDGE",EDGE,{"disambiguationData":[OSD([subQ3]),TDD([makeQuery(id+"F0.imprint","IMPRINT",EDGE,{"disambiguationData":[TD([[makeQuery(id+"F0.imprint","INTERSECT",VERTEX,{"derivedFrom":[subQ3,subQ1]}),-1.0]])],"derivedFrom":subQ3})])],"isStart":false}),makeQuery(id+"F3.opExtrude","CAP_FACE",FACE,{"disambiguationData":[OSD([subQ3,subQ2,subQ1,subQ0])],"isStart":false}),makeQuery(id+"F3.boolean.opBoolean","MERGE",FACE,{"derivedFrom":[makeQuery(id+"F2.opExtrude","SWEPT_FACE",FACE,{"disambiguationData":[OSD([subQ0])]}),makeQuery(id+"F3.opExtrude","SWEPT_FACE",FACE,{"disambiguationData":[OSD([subQ0])]})]})],"blendedInto":[makeQuery(id+"F3.opExtrude","CAP_FACE",FACE,{"disambiguationData":[OSD([subQ3,subQ2,subQ1,subQ0])],"isStart":false}),makeQuery(id+"F3.boolean.opBoolean","MERGE",FACE,{"derivedFrom":[makeQuery(id+"F2.opExtrude","SWEPT_FACE",FACE,{"disambiguationData":[OSD([subQ0])]}),makeQuery(id+"F3.opExtrude","SWEPT_FACE",FACE,{"disambiguationData":[OSD([subQ0])]})]})]});Q1=makeQuery(id+"F15.opExtrude","CAP_EDGE",EDGE,{"disambiguationData":[OSD([subQ3,subQ2,subQ1,subQ0]),TDD([makeQuery(id+"F12.boolean.opBoolean","MERGE",EDGE,{"derivedFrom":[makeQuery(id+"F11.opExtrude","SWEPT_EDGE",EDGE,{"disambiguationData":[OSD([subQ3,subQ2,subQ1,subQ0]),TDD([subQ4])]}),makeQuery(id+"F12.opExtrude","SWEPT_EDGE",EDGE,{"disambiguationData":[OSD([subQ3,subQ2,subQ1,subQ0]),TDD([makeQuery(id+"F11.opExtrude","CAP_VERTEX",VERTEX,{"disambiguationData":[OSD([subQ3,subQ2,subQ1,subQ0]),TDD([subQ4])],"isStart":false})])]})]})])],"isStart":false});}
            var Q2;
            {var subQ0=sQuery(id+"F0.wireOp",EDGE,"E25");var subQ1=sQuery(id+"F0.wireOp",EDGE,"E26");var subQ2=sQuery(id+"F0.wireOp",EDGE,"E21");var subQ3=sQuery(id+"F0.wireOp",EDGE,"E19");var subQ4=makeQuery(id+"F10.opChamfer","BLEND_VERTEX",VERTEX,{"blendedFrom":[makeQuery(id+"F3.opExtrude","CAP_EDGE",EDGE,{"disambiguationData":[OSD([subQ3]),TDD([makeQuery(id+"F0.imprint","IMPRINT",EDGE,{"disambiguationData":[TD([[makeQuery(id+"F0.imprint","INTERSECT",VERTEX,{"derivedFrom":[subQ3,subQ0]}),-1.0]])],"derivedFrom":subQ3})])],"isStart":false}),makeQuery(id+"F3.opExtrude","CAP_FACE",FACE,{"disambiguationData":[OSD([subQ3,subQ2,subQ0,subQ1])],"isStart":false}),makeQuery(id+"F3.boolean.opBoolean","MERGE",FACE,{"derivedFrom":[makeQuery(id+"F2.opExtrude","SWEPT_FACE",FACE,{"disambiguationData":[OSD([subQ0])]}),makeQuery(id+"F3.opExtrude","SWEPT_FACE",FACE,{"disambiguationData":[OSD([subQ0])]})]})],"blendedInto":[makeQuery(id+"F3.opExtrude","CAP_FACE",FACE,{"disambiguationData":[OSD([subQ3,subQ2,subQ0,subQ1])],"isStart":false}),makeQuery(id+"F3.boolean.opBoolean","MERGE",FACE,{"derivedFrom":[makeQuery(id+"F2.opExtrude","SWEPT_FACE",FACE,{"disambiguationData":[OSD([subQ0])]}),makeQuery(id+"F3.opExtrude","SWEPT_FACE",FACE,{"disambiguationData":[OSD([subQ0])]})]})]});Q2=makeQuery(id+"F15.opExtrude","CAP_EDGE",EDGE,{"disambiguationData":[OSD([subQ3,subQ2,subQ0,subQ1]),TDD([makeQuery(id+"F12.boolean.opBoolean","MERGE",EDGE,{"derivedFrom":[makeQuery(id+"F11.opExtrude","SWEPT_EDGE",EDGE,{"disambiguationData":[OSD([subQ3,subQ2,subQ0,subQ1]),TDD([subQ4])]}),makeQuery(id+"F12.opExtrude","SWEPT_EDGE",EDGE,{"disambiguationData":[OSD([subQ3,subQ2,subQ0,subQ1]),TDD([makeQuery(id+"F11.opExtrude","CAP_VERTEX",VERTEX,{"disambiguationData":[OSD([subQ3,subQ2,subQ0,subQ1]),TDD([subQ4])],"isStart":false})])]})]})])],"isStart":false});}
            var Q3;
            {var subQ0=sQuery(id+"F0.wireOp",EDGE,"E23");var subQ1=sQuery(id+"F0.wireOp",EDGE,"E29");var subQ2=sQuery(id+"F0.wireOp",EDGE,"E21");var subQ3=sQuery(id+"F0.wireOp",EDGE,"E19");var subQ4=makeQuery(id+"F10.opChamfer","BLEND_VERTEX",VERTEX,{"blendedFrom":[makeQuery(id+"F3.opExtrude","CAP_EDGE",EDGE,{"disambiguationData":[OSD([subQ3]),TDD([makeQuery(id+"F0.imprint","IMPRINT",EDGE,{"disambiguationData":[TD([[makeQuery(id+"F0.imprint","INTERSECT",VERTEX,{"derivedFrom":[subQ3,subQ1]}),-1.0]])],"derivedFrom":subQ3})])],"isStart":false}),makeQuery(id+"F3.opExtrude","CAP_FACE",FACE,{"disambiguationData":[OSD([subQ3,subQ2,subQ0,subQ1])],"isStart":false}),makeQuery(id+"F3.boolean.opBoolean","MERGE",FACE,{"derivedFrom":[makeQuery(id+"F2.opExtrude","SWEPT_FACE",FACE,{"disambiguationData":[OSD([subQ0])]}),makeQuery(id+"F3.opExtrude","SWEPT_FACE",FACE,{"disambiguationData":[OSD([subQ0])]})]})],"blendedInto":[makeQuery(id+"F3.opExtrude","CAP_FACE",FACE,{"disambiguationData":[OSD([subQ3,subQ2,subQ0,subQ1])],"isStart":false}),makeQuery(id+"F3.boolean.opBoolean","MERGE",FACE,{"derivedFrom":[makeQuery(id+"F2.opExtrude","SWEPT_FACE",FACE,{"disambiguationData":[OSD([subQ0])]}),makeQuery(id+"F3.opExtrude","SWEPT_FACE",FACE,{"disambiguationData":[OSD([subQ0])]})]})]});Q3=makeQuery(id+"F15.opExtrude","CAP_EDGE",EDGE,{"disambiguationData":[OSD([subQ3,subQ2,subQ0,subQ1]),TDD([makeQuery(id+"F12.boolean.opBoolean","MERGE",EDGE,{"derivedFrom":[makeQuery(id+"F11.opExtrude","SWEPT_EDGE",EDGE,{"disambiguationData":[OSD([subQ3,subQ2,subQ0,subQ1]),TDD([subQ4])]}),makeQuery(id+"F12.opExtrude","SWEPT_EDGE",EDGE,{"disambiguationData":[OSD([subQ3,subQ2,subQ0,subQ1]),TDD([makeQuery(id+"F11.opExtrude","CAP_VERTEX",VERTEX,{"disambiguationData":[OSD([subQ3,subQ2,subQ0,subQ1]),TDD([subQ4])],"isStart":false})])]})]})])],"isStart":false});}
            var Q4;
            {var subQ0=sQuery(id+"F0.wireOp",EDGE,"E29");var subQ1=sQuery(id+"F0.wireOp",EDGE,"E23");var subQ2=sQuery(id+"F0.wireOp",EDGE,"E21");var subQ3=sQuery(id+"F0.wireOp",EDGE,"E19");var subQ4=makeQuery(id+"F10.opChamfer","BLEND_VERTEX",VERTEX,{"blendedFrom":[makeQuery(id+"F3.opExtrude","CAP_EDGE",EDGE,{"disambiguationData":[OSD([subQ3]),TDD([makeQuery(id+"F0.imprint","IMPRINT",EDGE,{"disambiguationData":[TD([[makeQuery(id+"F0.imprint","INTERSECT",VERTEX,{"derivedFrom":[subQ3,subQ0]}),-1.0]])],"derivedFrom":subQ3})])],"isStart":false}),makeQuery(id+"F3.opExtrude","CAP_FACE",FACE,{"disambiguationData":[OSD([subQ3,subQ2,subQ1,subQ0])],"isStart":false}),makeQuery(id+"F3.boolean.opBoolean","MERGE",FACE,{"derivedFrom":[makeQuery(id+"F2.opExtrude","SWEPT_FACE",FACE,{"disambiguationData":[OSD([subQ0])]}),makeQuery(id+"F3.opExtrude","SWEPT_FACE",FACE,{"disambiguationData":[OSD([subQ0])]})]})],"blendedInto":[makeQuery(id+"F3.opExtrude","CAP_FACE",FACE,{"disambiguationData":[OSD([subQ3,subQ2,subQ1,subQ0])],"isStart":false}),makeQuery(id+"F3.boolean.opBoolean","MERGE",FACE,{"derivedFrom":[makeQuery(id+"F2.opExtrude","SWEPT_FACE",FACE,{"disambiguationData":[OSD([subQ0])]}),makeQuery(id+"F3.opExtrude","SWEPT_FACE",FACE,{"disambiguationData":[OSD([subQ0])]})]})]});Q4=makeQuery(id+"F15.opExtrude","CAP_EDGE",EDGE,{"disambiguationData":[OSD([subQ3,subQ2,subQ1,subQ0]),TDD([makeQuery(id+"F12.boolean.opBoolean","MERGE",EDGE,{"derivedFrom":[makeQuery(id+"F11.opExtrude","SWEPT_EDGE",EDGE,{"disambiguationData":[OSD([subQ3,subQ2,subQ1,subQ0]),TDD([subQ4])]}),makeQuery(id+"F12.opExtrude","SWEPT_EDGE",EDGE,{"disambiguationData":[OSD([subQ3,subQ2,subQ1,subQ0]),TDD([makeQuery(id+"F11.opExtrude","CAP_VERTEX",VERTEX,{"disambiguationData":[OSD([subQ3,subQ2,subQ1,subQ0]),TDD([subQ4])],"isStart":false})])]})]})])],"isStart":false});}
            var Q5;
            {var subQ0=sQuery(id+"F0.wireOp",EDGE,"E31");var subQ1=sQuery(id+"F0.wireOp",EDGE,"E21");var subQ2=sQuery(id+"F0.wireOp",EDGE,"E19");var subQ3=sQuery(id+"F0.wireOp",EDGE,"E18.top");var subQ4=makeQuery(id+"F10.opChamfer","BLEND_VERTEX",VERTEX,{"blendedFrom":[makeQuery(id+"F3.opExtrude","CAP_EDGE",EDGE,{"disambiguationData":[OSD([subQ2]),TDD([makeQuery(id+"F0.imprint","IMPRINT",EDGE,{"disambiguationData":[TD([[makeQuery(id+"F0.imprint","INTERSECT",VERTEX,{"derivedFrom":[subQ3,subQ2]}),-1.0]])],"derivedFrom":subQ2})])],"isStart":false}),makeQuery(id+"F3.opExtrude","CAP_FACE",FACE,{"disambiguationData":[OSD([subQ3,subQ2,subQ1,subQ0])],"isStart":false}),makeQuery(id+"F3.boolean.opBoolean","MERGE",FACE,{"derivedFrom":[makeQuery(id+"F2.opExtrude","SWEPT_FACE",FACE,{"disambiguationData":[OSD([subQ0])]}),makeQuery(id+"F3.opExtrude","SWEPT_FACE",FACE,{"disambiguationData":[OSD([subQ0])]})]})],"blendedInto":[makeQuery(id+"F3.opExtrude","CAP_FACE",FACE,{"disambiguationData":[OSD([subQ3,subQ2,subQ1,subQ0])],"isStart":false}),makeQuery(id+"F3.boolean.opBoolean","MERGE",FACE,{"derivedFrom":[makeQuery(id+"F2.opExtrude","SWEPT_FACE",FACE,{"disambiguationData":[OSD([subQ0])]}),makeQuery(id+"F3.opExtrude","SWEPT_FACE",FACE,{"disambiguationData":[OSD([subQ0])]})]})]});Q5=makeQuery(id+"F15.opExtrude","CAP_EDGE",EDGE,{"disambiguationData":[OSD([subQ3,subQ2,subQ1,subQ0]),TDD([makeQuery(id+"F12.boolean.opBoolean","MERGE",EDGE,{"derivedFrom":[makeQuery(id+"F11.opExtrude","SWEPT_EDGE",EDGE,{"disambiguationData":[OSD([subQ3,subQ2,subQ1,subQ0]),TDD([subQ4])]}),makeQuery(id+"F12.opExtrude","SWEPT_EDGE",EDGE,{"disambiguationData":[OSD([subQ3,subQ2,subQ1,subQ0]),TDD([makeQuery(id+"F11.opExtrude","CAP_VERTEX",VERTEX,{"disambiguationData":[OSD([subQ3,subQ2,subQ1,subQ0]),TDD([subQ4])],"isStart":false})])]})]})])],"isStart":false});}
            chamfer(context, id + "F20", {"entities" : qUnion([Q0, Q1, Q2, Q3, Q4, Q5]), "width" : 1 * mm});
        }
    });
